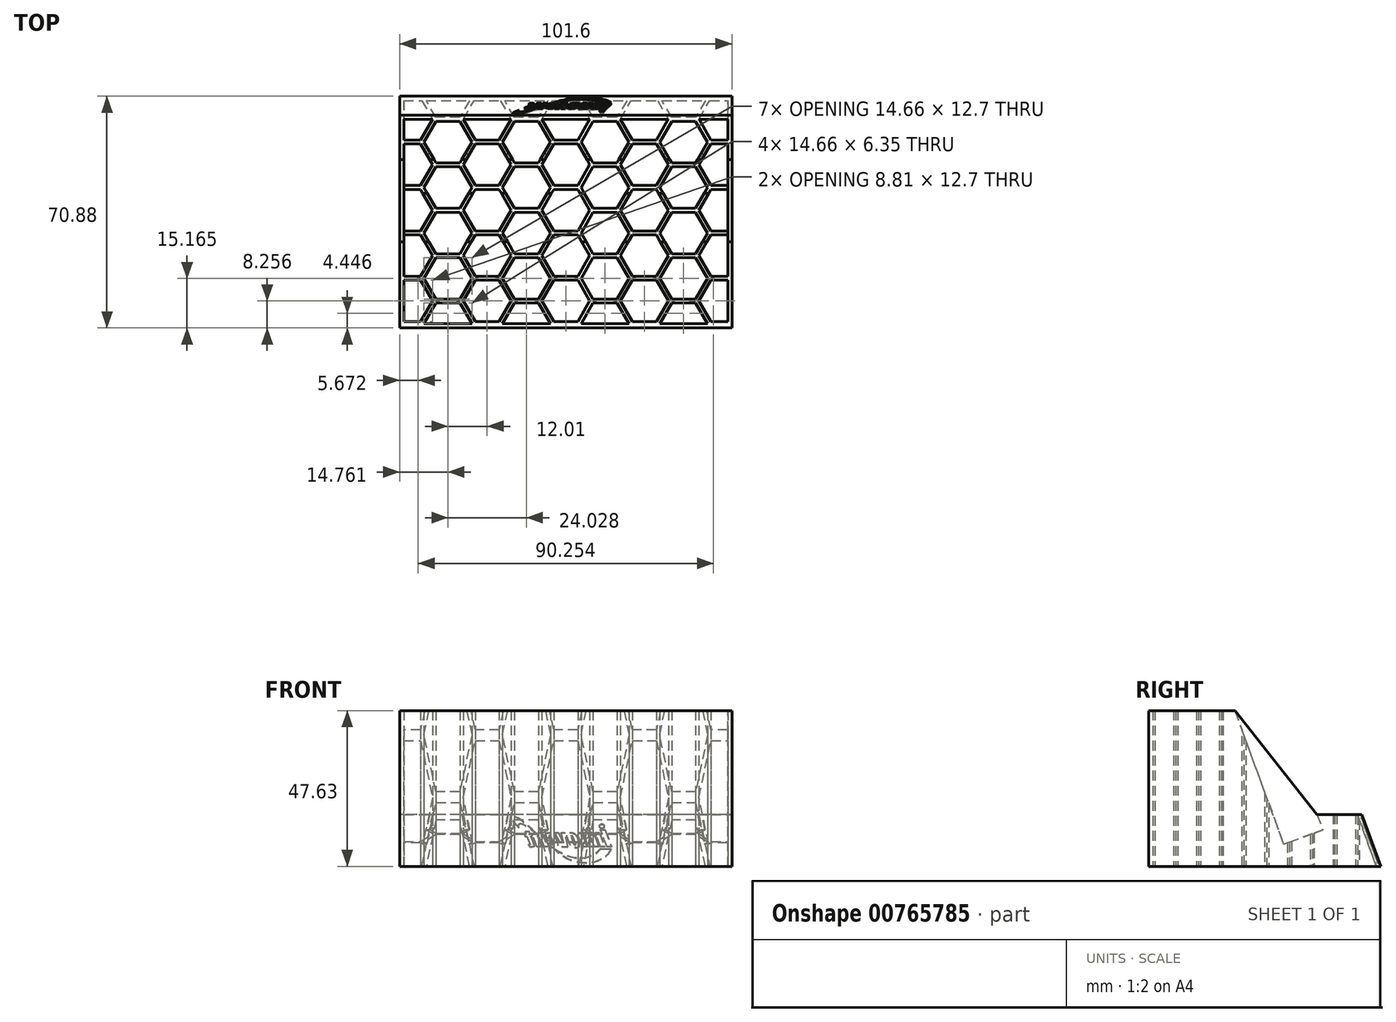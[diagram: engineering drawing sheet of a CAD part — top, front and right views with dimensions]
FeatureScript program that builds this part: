
annotation { "Feature Type Name" : "Feature", "Feature Type Description" : "" }
export const myFeature = defineFeature(function(context is Context, id is Id, definition is map)
    precondition{}
    {
        {
            var Q0;
            Q0=qCreatedBy(makeId("Top.planeOp"),FACE);
            var sketch = newSketch(context, id + "F0", { "sketchPlane" : qUnion([Q0])});
            skLineSegment(sketch, "E0.bottom", {"start": v(-69.85, 53.97) * mm, "end": v(69.85, 53.98) * mm});
            skLineSegment(sketch, "E0.top", {"start": v(-69.85, -47.63) * mm, "end": v(69.85, -47.62) * mm});
            skLineSegment(sketch, "E0.left", {"start": v(-69.85, 53.97) * mm, "end": v(-69.85, -47.63) * mm});
            skLineSegment(sketch, "E0.right", {"start": v(69.85, 53.98) * mm, "end": v(69.85, -47.62) * mm});
            skSolve(sketch);
        }
        {
            var Q0;
            Q0=makeQuery(id+"F0.imprint","IMPRINT",FACE,{"disambiguationData":[TD([[makeQuery(id+"F0.imprint","IMPRINT",EDGE,{"derivedFrom":sQuery(id+"F0.wireOp",EDGE,"E0.bottom")}),-1.0]])]});
            extrude(context, id + "F1", {"entities" : qUnion([Q0]), "depth" : 63.5 * mm, "offsetDistance" : 25.4 * mm});
        }
        {
            var Q0;
            Q0=qCreatedBy(makeId("Top.planeOp"),FACE);
            var sketch = newSketch(context, id + "F2", { "sketchPlane" : qUnion([Q0])});
            skCircle(sketch, "E1.cCircle", {"center": v(-61.25, 31.75) * mm, "radius": 6.35 * mm});
            skLineSegment(sketch, "E1.0", {"start": v(-57.58, 25.4) * mm, "end": v(-64.91, 25.4) * mm});
            skLineSegment(sketch, "E1.1", {"start": v(-64.91, 25.4) * mm, "end": v(-68.58, 31.75) * mm});
            skLineSegment(sketch, "E1.2", {"start": v(-68.58, 31.75) * mm, "end": v(-64.91, 38.1) * mm});
            skLineSegment(sketch, "E1.3", {"start": v(-64.91, 38.1) * mm, "end": v(-57.58, 38.1) * mm});
            skLineSegment(sketch, "E1.4", {"start": v(-57.58, 38.1) * mm, "end": v(-53.92, 31.75) * mm});
            skLineSegment(sketch, "E1.5", {"start": v(-53.92, 31.75) * mm, "end": v(-57.58, 25.4) * mm});
            skPoint(sketch, "E1.0.midPoint", {"position": v(-61.25, 25.4) * mm});
            skLineSegment(sketch, "E2.0.1.0", {"start": v(-64.91, 24.2) * mm, "end": v(-57.58, 24.2) * mm});
            skLineSegment(sketch, "E2.0.1.1", {"start": v(-68.58, 17.86) * mm, "end": v(-64.91, 24.2) * mm});
            skLineSegment(sketch, "E2.0.1.2", {"start": v(-64.91, 11.5) * mm, "end": v(-68.58, 17.86) * mm});
            skLineSegment(sketch, "E2.0.1.3", {"start": v(-57.58, 24.2) * mm, "end": v(-53.92, 17.86) * mm});
            skLineSegment(sketch, "E2.0.1.4", {"start": v(-53.92, 17.86) * mm, "end": v(-57.58, 11.5) * mm});
            skCircle(sketch, "E2.0.1.5", {"center": v(-61.25, 17.86) * mm, "radius": 6.35 * mm});
            skPoint(sketch, "E2.0.1.6", {"position": v(-61.25, 11.5) * mm});
            skLineSegment(sketch, "E2.0.1.7", {"start": v(-57.58, 11.5) * mm, "end": v(-64.91, 11.5) * mm});
            skLineSegment(sketch, "E2.0.2.0", {"start": v(-64.91, 10.31) * mm, "end": v(-57.58, 10.31) * mm});
            skLineSegment(sketch, "E2.0.2.1", {"start": v(-68.58, 3.96) * mm, "end": v(-64.91, 10.31) * mm});
            skLineSegment(sketch, "E2.0.2.2", {"start": v(-64.91, -2.39) * mm, "end": v(-68.58, 3.96) * mm});
            skLineSegment(sketch, "E2.0.2.3", {"start": v(-57.58, 10.31) * mm, "end": v(-53.92, 3.96) * mm});
            skLineSegment(sketch, "E2.0.2.4", {"start": v(-53.92, 3.96) * mm, "end": v(-57.58, -2.39) * mm});
            skCircle(sketch, "E2.0.2.5", {"center": v(-61.25, 3.96) * mm, "radius": 6.35 * mm});
            skPoint(sketch, "E2.0.2.6", {"position": v(-61.25, -2.39) * mm});
            skLineSegment(sketch, "E2.0.2.7", {"start": v(-57.58, -2.39) * mm, "end": v(-64.91, -2.39) * mm});
            skLineSegment(sketch, "E2.0.3.0", {"start": v(-64.91, -3.58) * mm, "end": v(-57.58, -3.58) * mm});
            skLineSegment(sketch, "E2.0.3.1", {"start": v(-68.58, -9.93) * mm, "end": v(-64.91, -3.58) * mm});
            skLineSegment(sketch, "E2.0.3.2", {"start": v(-64.91, -16.28) * mm, "end": v(-68.58, -9.93) * mm});
            skLineSegment(sketch, "E2.0.3.3", {"start": v(-57.58, -3.58) * mm, "end": v(-53.92, -9.93) * mm});
            skLineSegment(sketch, "E2.0.3.4", {"start": v(-53.92, -9.93) * mm, "end": v(-57.58, -16.28) * mm});
            skCircle(sketch, "E2.0.3.5", {"center": v(-61.25, -9.93) * mm, "radius": 6.35 * mm});
            skPoint(sketch, "E2.0.3.6", {"position": v(-61.25, -16.28) * mm});
            skLineSegment(sketch, "E2.0.3.7", {"start": v(-57.58, -16.28) * mm, "end": v(-64.91, -16.28) * mm});
            skLineSegment(sketch, "E2.0.4.0", {"start": v(-64.91, -17.48) * mm, "end": v(-57.58, -17.48) * mm});
            skLineSegment(sketch, "E2.0.4.1", {"start": v(-68.58, -23.83) * mm, "end": v(-64.91, -17.48) * mm});
            skLineSegment(sketch, "E2.0.4.2", {"start": v(-64.91, -30.18) * mm, "end": v(-68.58, -23.83) * mm});
            skLineSegment(sketch, "E2.0.4.3", {"start": v(-57.58, -17.48) * mm, "end": v(-53.92, -23.83) * mm});
            skLineSegment(sketch, "E2.0.4.4", {"start": v(-53.92, -23.83) * mm, "end": v(-57.58, -30.18) * mm});
            skCircle(sketch, "E2.0.4.5", {"center": v(-61.25, -23.83) * mm, "radius": 6.35 * mm});
            skPoint(sketch, "E2.0.4.6", {"position": v(-61.25, -30.18) * mm});
            skLineSegment(sketch, "E2.0.4.7", {"start": v(-57.58, -30.18) * mm, "end": v(-64.91, -30.18) * mm});
            skLineSegment(sketch, "E2.0.5.0", {"start": v(-64.91, -31.37) * mm, "end": v(-57.58, -31.37) * mm});
            skLineSegment(sketch, "E2.0.5.1", {"start": v(-68.58, -37.72) * mm, "end": v(-64.91, -31.37) * mm});
            skLineSegment(sketch, "E2.0.5.2", {"start": v(-64.91, -44.07) * mm, "end": v(-68.58, -37.72) * mm});
            skLineSegment(sketch, "E2.0.5.3", {"start": v(-57.58, -31.37) * mm, "end": v(-53.92, -37.72) * mm});
            skLineSegment(sketch, "E2.0.5.4", {"start": v(-53.92, -37.72) * mm, "end": v(-57.58, -44.07) * mm});
            skCircle(sketch, "E2.0.5.5", {"center": v(-61.25, -37.72) * mm, "radius": 6.35 * mm});
            skPoint(sketch, "E2.0.5.6", {"position": v(-61.25, -44.07) * mm});
            skLineSegment(sketch, "E2.0.5.7", {"start": v(-57.58, -44.07) * mm, "end": v(-64.91, -44.07) * mm});
            skLineSegment(sketch, "E2.1.0.0", {"start": v(-40.89, 38.1) * mm, "end": v(-33.55, 38.1) * mm});
            skLineSegment(sketch, "E2.1.0.1", {"start": v(-44.55, 31.75) * mm, "end": v(-40.89, 38.1) * mm});
            skLineSegment(sketch, "E2.1.0.2", {"start": v(-40.89, 25.4) * mm, "end": v(-44.55, 31.75) * mm});
            skLineSegment(sketch, "E2.1.0.3", {"start": v(-33.55, 38.1) * mm, "end": v(-29.89, 31.75) * mm});
            skLineSegment(sketch, "E2.1.0.4", {"start": v(-29.89, 31.75) * mm, "end": v(-33.55, 25.4) * mm});
            skCircle(sketch, "E2.1.0.5", {"center": v(-37.22, 31.75) * mm, "radius": 6.35 * mm});
            skPoint(sketch, "E2.1.0.6", {"position": v(-37.22, 25.4) * mm});
            skLineSegment(sketch, "E2.1.0.7", {"start": v(-33.55, 25.4) * mm, "end": v(-40.89, 25.4) * mm});
            skLineSegment(sketch, "E2.1.1.0", {"start": v(-40.89, 24.2) * mm, "end": v(-33.55, 24.2) * mm});
            skLineSegment(sketch, "E2.1.1.1", {"start": v(-44.55, 17.86) * mm, "end": v(-40.89, 24.2) * mm});
            skLineSegment(sketch, "E2.1.1.2", {"start": v(-40.89, 11.5) * mm, "end": v(-44.55, 17.86) * mm});
            skLineSegment(sketch, "E2.1.1.3", {"start": v(-33.55, 24.2) * mm, "end": v(-29.89, 17.86) * mm});
            skLineSegment(sketch, "E2.1.1.4", {"start": v(-29.89, 17.86) * mm, "end": v(-33.55, 11.5) * mm});
            skCircle(sketch, "E2.1.1.5", {"center": v(-37.22, 17.86) * mm, "radius": 6.35 * mm});
            skPoint(sketch, "E2.1.1.6", {"position": v(-37.22, 11.5) * mm});
            skLineSegment(sketch, "E2.1.1.7", {"start": v(-33.55, 11.5) * mm, "end": v(-40.89, 11.5) * mm});
            skLineSegment(sketch, "E2.1.2.0", {"start": v(-40.89, 10.31) * mm, "end": v(-33.55, 10.31) * mm});
            skLineSegment(sketch, "E2.1.2.1", {"start": v(-44.55, 3.96) * mm, "end": v(-40.89, 10.31) * mm});
            skLineSegment(sketch, "E2.1.2.2", {"start": v(-40.89, -2.39) * mm, "end": v(-44.55, 3.96) * mm});
            skLineSegment(sketch, "E2.1.2.3", {"start": v(-33.55, 10.31) * mm, "end": v(-29.89, 3.96) * mm});
            skLineSegment(sketch, "E2.1.2.4", {"start": v(-29.89, 3.96) * mm, "end": v(-33.55, -2.39) * mm});
            skCircle(sketch, "E2.1.2.5", {"center": v(-37.22, 3.96) * mm, "radius": 6.35 * mm});
            skPoint(sketch, "E2.1.2.6", {"position": v(-37.22, -2.39) * mm});
            skLineSegment(sketch, "E2.1.2.7", {"start": v(-33.55, -2.39) * mm, "end": v(-40.89, -2.39) * mm});
            skLineSegment(sketch, "E2.1.3.0", {"start": v(-40.89, -3.58) * mm, "end": v(-33.55, -3.58) * mm});
            skLineSegment(sketch, "E2.1.3.1", {"start": v(-44.55, -9.93) * mm, "end": v(-40.89, -3.58) * mm});
            skLineSegment(sketch, "E2.1.3.2", {"start": v(-40.89, -16.28) * mm, "end": v(-44.55, -9.93) * mm});
            skLineSegment(sketch, "E2.1.3.3", {"start": v(-33.55, -3.58) * mm, "end": v(-29.89, -9.93) * mm});
            skLineSegment(sketch, "E2.1.3.4", {"start": v(-29.89, -9.93) * mm, "end": v(-33.55, -16.28) * mm});
            skCircle(sketch, "E2.1.3.5", {"center": v(-37.22, -9.93) * mm, "radius": 6.35 * mm});
            skPoint(sketch, "E2.1.3.6", {"position": v(-37.22, -16.28) * mm});
            skLineSegment(sketch, "E2.1.3.7", {"start": v(-33.55, -16.28) * mm, "end": v(-40.89, -16.28) * mm});
            skLineSegment(sketch, "E2.1.4.0", {"start": v(-40.89, -17.48) * mm, "end": v(-33.55, -17.48) * mm});
            skLineSegment(sketch, "E2.1.4.1", {"start": v(-44.55, -23.83) * mm, "end": v(-40.89, -17.48) * mm});
            skLineSegment(sketch, "E2.1.4.2", {"start": v(-40.89, -30.18) * mm, "end": v(-44.55, -23.83) * mm});
            skLineSegment(sketch, "E2.1.4.3", {"start": v(-33.55, -17.48) * mm, "end": v(-29.89, -23.83) * mm});
            skLineSegment(sketch, "E2.1.4.4", {"start": v(-29.89, -23.83) * mm, "end": v(-33.55, -30.18) * mm});
            skCircle(sketch, "E2.1.4.5", {"center": v(-37.22, -23.83) * mm, "radius": 6.35 * mm});
            skPoint(sketch, "E2.1.4.6", {"position": v(-37.22, -30.18) * mm});
            skLineSegment(sketch, "E2.1.4.7", {"start": v(-33.55, -30.18) * mm, "end": v(-40.89, -30.18) * mm});
            skLineSegment(sketch, "E2.1.5.0", {"start": v(-40.89, -31.37) * mm, "end": v(-33.55, -31.37) * mm});
            skLineSegment(sketch, "E2.1.5.1", {"start": v(-44.55, -37.72) * mm, "end": v(-40.89, -31.37) * mm});
            skLineSegment(sketch, "E2.1.5.2", {"start": v(-40.89, -44.07) * mm, "end": v(-44.55, -37.72) * mm});
            skLineSegment(sketch, "E2.1.5.3", {"start": v(-33.55, -31.37) * mm, "end": v(-29.89, -37.72) * mm});
            skLineSegment(sketch, "E2.1.5.4", {"start": v(-29.89, -37.72) * mm, "end": v(-33.55, -44.07) * mm});
            skCircle(sketch, "E2.1.5.5", {"center": v(-37.22, -37.72) * mm, "radius": 6.35 * mm});
            skPoint(sketch, "E2.1.5.6", {"position": v(-37.22, -44.07) * mm});
            skLineSegment(sketch, "E2.1.5.7", {"start": v(-33.55, -44.07) * mm, "end": v(-40.89, -44.07) * mm});
            skLineSegment(sketch, "E2.2.0.0", {"start": v(-16.86, 38.1) * mm, "end": v(-9.52, 38.1) * mm});
            skLineSegment(sketch, "E2.2.0.1", {"start": v(-20.52, 31.75) * mm, "end": v(-16.86, 38.1) * mm});
            skLineSegment(sketch, "E2.2.0.2", {"start": v(-16.86, 25.4) * mm, "end": v(-20.52, 31.75) * mm});
            skLineSegment(sketch, "E2.2.0.3", {"start": v(-9.52, 38.1) * mm, "end": v(-5.86, 31.75) * mm});
            skLineSegment(sketch, "E2.2.0.4", {"start": v(-5.86, 31.75) * mm, "end": v(-9.52, 25.4) * mm});
            skCircle(sketch, "E2.2.0.5", {"center": v(-13.2, 31.75) * mm, "radius": 6.35 * mm});
            skPoint(sketch, "E2.2.0.6", {"position": v(-13.2, 25.4) * mm});
            skLineSegment(sketch, "E2.2.0.7", {"start": v(-9.52, 25.4) * mm, "end": v(-16.86, 25.4) * mm});
            skLineSegment(sketch, "E2.2.1.0", {"start": v(-16.86, 24.2) * mm, "end": v(-9.52, 24.2) * mm});
            skLineSegment(sketch, "E2.2.1.1", {"start": v(-20.52, 17.86) * mm, "end": v(-16.86, 24.2) * mm});
            skLineSegment(sketch, "E2.2.1.2", {"start": v(-16.86, 11.5) * mm, "end": v(-20.52, 17.86) * mm});
            skLineSegment(sketch, "E2.2.1.3", {"start": v(-9.52, 24.2) * mm, "end": v(-5.86, 17.86) * mm});
            skLineSegment(sketch, "E2.2.1.4", {"start": v(-5.86, 17.86) * mm, "end": v(-9.52, 11.5) * mm});
            skCircle(sketch, "E2.2.1.5", {"center": v(-13.2, 17.86) * mm, "radius": 6.35 * mm});
            skPoint(sketch, "E2.2.1.6", {"position": v(-13.2, 11.5) * mm});
            skLineSegment(sketch, "E2.2.1.7", {"start": v(-9.52, 11.5) * mm, "end": v(-16.86, 11.5) * mm});
            skLineSegment(sketch, "E2.2.2.0", {"start": v(-16.86, 10.31) * mm, "end": v(-9.52, 10.31) * mm});
            skLineSegment(sketch, "E2.2.2.1", {"start": v(-20.52, 3.96) * mm, "end": v(-16.86, 10.31) * mm});
            skLineSegment(sketch, "E2.2.2.2", {"start": v(-16.86, -2.39) * mm, "end": v(-20.52, 3.96) * mm});
            skLineSegment(sketch, "E2.2.2.3", {"start": v(-9.52, 10.31) * mm, "end": v(-5.86, 3.96) * mm});
            skLineSegment(sketch, "E2.2.2.4", {"start": v(-5.86, 3.96) * mm, "end": v(-9.52, -2.39) * mm});
            skCircle(sketch, "E2.2.2.5", {"center": v(-13.2, 3.96) * mm, "radius": 6.35 * mm});
            skPoint(sketch, "E2.2.2.6", {"position": v(-13.2, -2.39) * mm});
            skLineSegment(sketch, "E2.2.2.7", {"start": v(-9.52, -2.39) * mm, "end": v(-16.86, -2.39) * mm});
            skLineSegment(sketch, "E2.2.3.0", {"start": v(-16.86, -3.58) * mm, "end": v(-9.52, -3.58) * mm});
            skLineSegment(sketch, "E2.2.3.1", {"start": v(-20.52, -9.93) * mm, "end": v(-16.86, -3.58) * mm});
            skLineSegment(sketch, "E2.2.3.2", {"start": v(-16.86, -16.28) * mm, "end": v(-20.52, -9.93) * mm});
            skLineSegment(sketch, "E2.2.3.3", {"start": v(-9.52, -3.58) * mm, "end": v(-5.86, -9.93) * mm});
            skLineSegment(sketch, "E2.2.3.4", {"start": v(-5.86, -9.93) * mm, "end": v(-9.52, -16.28) * mm});
            skCircle(sketch, "E2.2.3.5", {"center": v(-13.2, -9.93) * mm, "radius": 6.35 * mm});
            skPoint(sketch, "E2.2.3.6", {"position": v(-13.2, -16.28) * mm});
            skLineSegment(sketch, "E2.2.3.7", {"start": v(-9.52, -16.28) * mm, "end": v(-16.86, -16.28) * mm});
            skLineSegment(sketch, "E2.2.4.0", {"start": v(-16.86, -17.48) * mm, "end": v(-9.52, -17.48) * mm});
            skLineSegment(sketch, "E2.2.4.1", {"start": v(-20.52, -23.83) * mm, "end": v(-16.86, -17.48) * mm});
            skLineSegment(sketch, "E2.2.4.2", {"start": v(-16.86, -30.18) * mm, "end": v(-20.52, -23.83) * mm});
            skLineSegment(sketch, "E2.2.4.3", {"start": v(-9.52, -17.48) * mm, "end": v(-5.86, -23.83) * mm});
            skLineSegment(sketch, "E2.2.4.4", {"start": v(-5.86, -23.83) * mm, "end": v(-9.52, -30.18) * mm});
            skCircle(sketch, "E2.2.4.5", {"center": v(-13.2, -23.83) * mm, "radius": 6.35 * mm});
            skPoint(sketch, "E2.2.4.6", {"position": v(-13.2, -30.18) * mm});
            skLineSegment(sketch, "E2.2.4.7", {"start": v(-9.52, -30.18) * mm, "end": v(-16.86, -30.18) * mm});
            skLineSegment(sketch, "E2.2.5.0", {"start": v(-16.86, -31.37) * mm, "end": v(-9.52, -31.37) * mm});
            skLineSegment(sketch, "E2.2.5.1", {"start": v(-20.52, -37.72) * mm, "end": v(-16.86, -31.37) * mm});
            skLineSegment(sketch, "E2.2.5.2", {"start": v(-16.86, -44.07) * mm, "end": v(-20.52, -37.72) * mm});
            skLineSegment(sketch, "E2.2.5.3", {"start": v(-9.52, -31.37) * mm, "end": v(-5.86, -37.72) * mm});
            skLineSegment(sketch, "E2.2.5.4", {"start": v(-5.86, -37.72) * mm, "end": v(-9.52, -44.07) * mm});
            skCircle(sketch, "E2.2.5.5", {"center": v(-13.2, -37.72) * mm, "radius": 6.35 * mm});
            skPoint(sketch, "E2.2.5.6", {"position": v(-13.2, -44.07) * mm});
            skLineSegment(sketch, "E2.2.5.7", {"start": v(-9.52, -44.07) * mm, "end": v(-16.86, -44.07) * mm});
            skLineSegment(sketch, "E2.3.0.0", {"start": v(7.17, 38.1) * mm, "end": v(14.5, 38.1) * mm});
            skLineSegment(sketch, "E2.3.0.1", {"start": v(3.5, 31.75) * mm, "end": v(7.17, 38.1) * mm});
            skLineSegment(sketch, "E2.3.0.2", {"start": v(7.17, 25.4) * mm, "end": v(3.5, 31.75) * mm});
            skLineSegment(sketch, "E2.3.0.3", {"start": v(14.5, 38.1) * mm, "end": v(18.17, 31.75) * mm});
            skLineSegment(sketch, "E2.3.0.4", {"start": v(18.17, 31.75) * mm, "end": v(14.5, 25.4) * mm});
            skCircle(sketch, "E2.3.0.5", {"center": v(10.84, 31.75) * mm, "radius": 6.35 * mm});
            skPoint(sketch, "E2.3.0.6", {"position": v(10.84, 25.4) * mm});
            skLineSegment(sketch, "E2.3.0.7", {"start": v(14.5, 25.4) * mm, "end": v(7.17, 25.4) * mm});
            skLineSegment(sketch, "E2.3.1.0", {"start": v(7.17, 24.2) * mm, "end": v(14.5, 24.2) * mm});
            skLineSegment(sketch, "E2.3.1.1", {"start": v(3.5, 17.86) * mm, "end": v(7.17, 24.2) * mm});
            skLineSegment(sketch, "E2.3.1.2", {"start": v(7.17, 11.5) * mm, "end": v(3.5, 17.86) * mm});
            skLineSegment(sketch, "E2.3.1.3", {"start": v(14.5, 24.2) * mm, "end": v(18.17, 17.86) * mm});
            skLineSegment(sketch, "E2.3.1.4", {"start": v(18.17, 17.86) * mm, "end": v(14.5, 11.5) * mm});
            skCircle(sketch, "E2.3.1.5", {"center": v(10.84, 17.86) * mm, "radius": 6.35 * mm});
            skPoint(sketch, "E2.3.1.6", {"position": v(10.84, 11.5) * mm});
            skLineSegment(sketch, "E2.3.1.7", {"start": v(14.5, 11.5) * mm, "end": v(7.17, 11.5) * mm});
            skLineSegment(sketch, "E2.3.2.0", {"start": v(7.17, 10.31) * mm, "end": v(14.5, 10.31) * mm});
            skLineSegment(sketch, "E2.3.2.1", {"start": v(3.5, 3.96) * mm, "end": v(7.17, 10.31) * mm});
            skLineSegment(sketch, "E2.3.2.2", {"start": v(7.17, -2.39) * mm, "end": v(3.5, 3.96) * mm});
            skLineSegment(sketch, "E2.3.2.3", {"start": v(14.5, 10.31) * mm, "end": v(18.17, 3.96) * mm});
            skLineSegment(sketch, "E2.3.2.4", {"start": v(18.17, 3.96) * mm, "end": v(14.5, -2.39) * mm});
            skCircle(sketch, "E2.3.2.5", {"center": v(10.84, 3.96) * mm, "radius": 6.35 * mm});
            skPoint(sketch, "E2.3.2.6", {"position": v(10.84, -2.39) * mm});
            skLineSegment(sketch, "E2.3.2.7", {"start": v(14.5, -2.39) * mm, "end": v(7.17, -2.39) * mm});
            skLineSegment(sketch, "E2.3.3.0", {"start": v(7.17, -3.58) * mm, "end": v(14.5, -3.58) * mm});
            skLineSegment(sketch, "E2.3.3.1", {"start": v(3.5, -9.93) * mm, "end": v(7.17, -3.58) * mm});
            skLineSegment(sketch, "E2.3.3.2", {"start": v(7.17, -16.28) * mm, "end": v(3.5, -9.93) * mm});
            skLineSegment(sketch, "E2.3.3.3", {"start": v(14.5, -3.58) * mm, "end": v(18.17, -9.93) * mm});
            skLineSegment(sketch, "E2.3.3.4", {"start": v(18.17, -9.93) * mm, "end": v(14.5, -16.28) * mm});
            skCircle(sketch, "E2.3.3.5", {"center": v(10.84, -9.93) * mm, "radius": 6.35 * mm});
            skPoint(sketch, "E2.3.3.6", {"position": v(10.84, -16.28) * mm});
            skLineSegment(sketch, "E2.3.3.7", {"start": v(14.5, -16.28) * mm, "end": v(7.17, -16.28) * mm});
            skLineSegment(sketch, "E2.3.4.0", {"start": v(7.17, -17.48) * mm, "end": v(14.5, -17.48) * mm});
            skLineSegment(sketch, "E2.3.4.1", {"start": v(3.5, -23.83) * mm, "end": v(7.17, -17.48) * mm});
            skLineSegment(sketch, "E2.3.4.2", {"start": v(7.17, -30.18) * mm, "end": v(3.5, -23.83) * mm});
            skLineSegment(sketch, "E2.3.4.3", {"start": v(14.5, -17.48) * mm, "end": v(18.17, -23.83) * mm});
            skLineSegment(sketch, "E2.3.4.4", {"start": v(18.17, -23.83) * mm, "end": v(14.5, -30.18) * mm});
            skCircle(sketch, "E2.3.4.5", {"center": v(10.84, -23.83) * mm, "radius": 6.35 * mm});
            skPoint(sketch, "E2.3.4.6", {"position": v(10.84, -30.18) * mm});
            skLineSegment(sketch, "E2.3.4.7", {"start": v(14.5, -30.18) * mm, "end": v(7.17, -30.18) * mm});
            skLineSegment(sketch, "E2.3.5.0", {"start": v(7.17, -31.37) * mm, "end": v(14.5, -31.37) * mm});
            skLineSegment(sketch, "E2.3.5.1", {"start": v(3.5, -37.72) * mm, "end": v(7.17, -31.37) * mm});
            skLineSegment(sketch, "E2.3.5.2", {"start": v(7.17, -44.07) * mm, "end": v(3.5, -37.72) * mm});
            skLineSegment(sketch, "E2.3.5.3", {"start": v(14.5, -31.37) * mm, "end": v(18.17, -37.72) * mm});
            skLineSegment(sketch, "E2.3.5.4", {"start": v(18.17, -37.72) * mm, "end": v(14.5, -44.07) * mm});
            skCircle(sketch, "E2.3.5.5", {"center": v(10.84, -37.72) * mm, "radius": 6.35 * mm});
            skPoint(sketch, "E2.3.5.6", {"position": v(10.84, -44.07) * mm});
            skLineSegment(sketch, "E2.3.5.7", {"start": v(14.5, -44.07) * mm, "end": v(7.17, -44.07) * mm});
            skLineSegment(sketch, "E2.4.0.0", {"start": v(31.2, 38.1) * mm, "end": v(38.53, 38.1) * mm});
            skLineSegment(sketch, "E2.4.0.1", {"start": v(27.53, 31.75) * mm, "end": v(31.2, 38.1) * mm});
            skLineSegment(sketch, "E2.4.0.2", {"start": v(31.2, 25.4) * mm, "end": v(27.53, 31.75) * mm});
            skLineSegment(sketch, "E2.4.0.3", {"start": v(38.53, 38.1) * mm, "end": v(42.2, 31.75) * mm});
            skLineSegment(sketch, "E2.4.0.4", {"start": v(42.2, 31.75) * mm, "end": v(38.53, 25.4) * mm});
            skCircle(sketch, "E2.4.0.5", {"center": v(34.87, 31.75) * mm, "radius": 6.35 * mm});
            skPoint(sketch, "E2.4.0.6", {"position": v(34.87, 25.4) * mm});
            skLineSegment(sketch, "E2.4.0.7", {"start": v(38.53, 25.4) * mm, "end": v(31.2, 25.4) * mm});
            skLineSegment(sketch, "E2.4.1.0", {"start": v(31.2, 24.2) * mm, "end": v(38.53, 24.2) * mm});
            skLineSegment(sketch, "E2.4.1.1", {"start": v(27.53, 17.86) * mm, "end": v(31.2, 24.2) * mm});
            skLineSegment(sketch, "E2.4.1.2", {"start": v(31.2, 11.5) * mm, "end": v(27.53, 17.86) * mm});
            skLineSegment(sketch, "E2.4.1.3", {"start": v(38.53, 24.2) * mm, "end": v(42.2, 17.86) * mm});
            skLineSegment(sketch, "E2.4.1.4", {"start": v(42.2, 17.86) * mm, "end": v(38.53, 11.5) * mm});
            skCircle(sketch, "E2.4.1.5", {"center": v(34.87, 17.86) * mm, "radius": 6.35 * mm});
            skPoint(sketch, "E2.4.1.6", {"position": v(34.87, 11.5) * mm});
            skLineSegment(sketch, "E2.4.1.7", {"start": v(38.53, 11.5) * mm, "end": v(31.2, 11.5) * mm});
            skLineSegment(sketch, "E2.4.2.0", {"start": v(31.2, 10.31) * mm, "end": v(38.53, 10.31) * mm});
            skLineSegment(sketch, "E2.4.2.1", {"start": v(27.53, 3.96) * mm, "end": v(31.2, 10.31) * mm});
            skLineSegment(sketch, "E2.4.2.2", {"start": v(31.2, -2.39) * mm, "end": v(27.53, 3.96) * mm});
            skLineSegment(sketch, "E2.4.2.3", {"start": v(38.53, 10.31) * mm, "end": v(42.2, 3.96) * mm});
            skLineSegment(sketch, "E2.4.2.4", {"start": v(42.2, 3.96) * mm, "end": v(38.53, -2.39) * mm});
            skCircle(sketch, "E2.4.2.5", {"center": v(34.87, 3.96) * mm, "radius": 6.35 * mm});
            skPoint(sketch, "E2.4.2.6", {"position": v(34.87, -2.39) * mm});
            skLineSegment(sketch, "E2.4.2.7", {"start": v(38.53, -2.39) * mm, "end": v(31.2, -2.39) * mm});
            skLineSegment(sketch, "E2.4.3.0", {"start": v(31.2, -3.58) * mm, "end": v(38.53, -3.58) * mm});
            skLineSegment(sketch, "E2.4.3.1", {"start": v(27.53, -9.93) * mm, "end": v(31.2, -3.58) * mm});
            skLineSegment(sketch, "E2.4.3.2", {"start": v(31.2, -16.28) * mm, "end": v(27.53, -9.93) * mm});
            skLineSegment(sketch, "E2.4.3.3", {"start": v(38.53, -3.58) * mm, "end": v(42.2, -9.93) * mm});
            skLineSegment(sketch, "E2.4.3.4", {"start": v(42.2, -9.93) * mm, "end": v(38.53, -16.28) * mm});
            skCircle(sketch, "E2.4.3.5", {"center": v(34.87, -9.93) * mm, "radius": 6.35 * mm});
            skPoint(sketch, "E2.4.3.6", {"position": v(34.87, -16.28) * mm});
            skLineSegment(sketch, "E2.4.3.7", {"start": v(38.53, -16.28) * mm, "end": v(31.2, -16.28) * mm});
            skLineSegment(sketch, "E2.4.4.0", {"start": v(31.2, -17.48) * mm, "end": v(38.53, -17.48) * mm});
            skLineSegment(sketch, "E2.4.4.1", {"start": v(27.53, -23.83) * mm, "end": v(31.2, -17.48) * mm});
            skLineSegment(sketch, "E2.4.4.2", {"start": v(31.2, -30.18) * mm, "end": v(27.53, -23.83) * mm});
            skLineSegment(sketch, "E2.4.4.3", {"start": v(38.53, -17.48) * mm, "end": v(42.2, -23.83) * mm});
            skLineSegment(sketch, "E2.4.4.4", {"start": v(42.2, -23.83) * mm, "end": v(38.53, -30.18) * mm});
            skCircle(sketch, "E2.4.4.5", {"center": v(34.87, -23.83) * mm, "radius": 6.35 * mm});
            skPoint(sketch, "E2.4.4.6", {"position": v(34.87, -30.18) * mm});
            skLineSegment(sketch, "E2.4.4.7", {"start": v(38.53, -30.18) * mm, "end": v(31.2, -30.18) * mm});
            skLineSegment(sketch, "E2.4.5.0", {"start": v(31.2, -31.37) * mm, "end": v(38.53, -31.37) * mm});
            skLineSegment(sketch, "E2.4.5.1", {"start": v(27.53, -37.72) * mm, "end": v(31.2, -31.37) * mm});
            skLineSegment(sketch, "E2.4.5.2", {"start": v(31.2, -44.07) * mm, "end": v(27.53, -37.72) * mm});
            skLineSegment(sketch, "E2.4.5.3", {"start": v(38.53, -31.37) * mm, "end": v(42.2, -37.72) * mm});
            skLineSegment(sketch, "E2.4.5.4", {"start": v(42.2, -37.72) * mm, "end": v(38.53, -44.07) * mm});
            skCircle(sketch, "E2.4.5.5", {"center": v(34.87, -37.72) * mm, "radius": 6.35 * mm});
            skPoint(sketch, "E2.4.5.6", {"position": v(34.87, -44.07) * mm});
            skLineSegment(sketch, "E2.4.5.7", {"start": v(38.53, -44.07) * mm, "end": v(31.2, -44.07) * mm});
            skLineSegment(sketch, "E2.5.0.0", {"start": v(55.23, 38.1) * mm, "end": v(62.56, 38.1) * mm});
            skLineSegment(sketch, "E2.5.0.1", {"start": v(51.56, 31.75) * mm, "end": v(55.23, 38.1) * mm});
            skLineSegment(sketch, "E2.5.0.2", {"start": v(55.23, 25.4) * mm, "end": v(51.56, 31.75) * mm});
            skLineSegment(sketch, "E2.5.0.3", {"start": v(62.56, 38.1) * mm, "end": v(66.23, 31.75) * mm});
            skLineSegment(sketch, "E2.5.0.4", {"start": v(66.23, 31.75) * mm, "end": v(62.56, 25.4) * mm});
            skCircle(sketch, "E2.5.0.5", {"center": v(58.9, 31.75) * mm, "radius": 6.35 * mm});
            skPoint(sketch, "E2.5.0.6", {"position": v(58.9, 25.4) * mm});
            skLineSegment(sketch, "E2.5.0.7", {"start": v(62.56, 25.4) * mm, "end": v(55.23, 25.4) * mm});
            skLineSegment(sketch, "E2.5.1.0", {"start": v(55.23, 24.2) * mm, "end": v(62.56, 24.2) * mm});
            skLineSegment(sketch, "E2.5.1.1", {"start": v(51.56, 17.86) * mm, "end": v(55.23, 24.2) * mm});
            skLineSegment(sketch, "E2.5.1.2", {"start": v(55.23, 11.5) * mm, "end": v(51.56, 17.86) * mm});
            skLineSegment(sketch, "E2.5.1.3", {"start": v(62.56, 24.2) * mm, "end": v(66.23, 17.86) * mm});
            skLineSegment(sketch, "E2.5.1.4", {"start": v(66.23, 17.86) * mm, "end": v(62.56, 11.5) * mm});
            skCircle(sketch, "E2.5.1.5", {"center": v(58.9, 17.86) * mm, "radius": 6.35 * mm});
            skPoint(sketch, "E2.5.1.6", {"position": v(58.9, 11.5) * mm});
            skLineSegment(sketch, "E2.5.1.7", {"start": v(62.56, 11.5) * mm, "end": v(55.23, 11.5) * mm});
            skLineSegment(sketch, "E2.5.2.0", {"start": v(55.23, 10.31) * mm, "end": v(62.56, 10.31) * mm});
            skLineSegment(sketch, "E2.5.2.1", {"start": v(51.56, 3.96) * mm, "end": v(55.23, 10.31) * mm});
            skLineSegment(sketch, "E2.5.2.2", {"start": v(55.23, -2.39) * mm, "end": v(51.56, 3.96) * mm});
            skLineSegment(sketch, "E2.5.2.3", {"start": v(62.56, 10.31) * mm, "end": v(66.23, 3.96) * mm});
            skLineSegment(sketch, "E2.5.2.4", {"start": v(66.23, 3.96) * mm, "end": v(62.56, -2.39) * mm});
            skCircle(sketch, "E2.5.2.5", {"center": v(58.9, 3.96) * mm, "radius": 6.35 * mm});
            skPoint(sketch, "E2.5.2.6", {"position": v(58.9, -2.39) * mm});
            skLineSegment(sketch, "E2.5.2.7", {"start": v(62.56, -2.39) * mm, "end": v(55.23, -2.39) * mm});
            skLineSegment(sketch, "E2.5.3.0", {"start": v(55.23, -3.58) * mm, "end": v(62.56, -3.58) * mm});
            skLineSegment(sketch, "E2.5.3.1", {"start": v(51.56, -9.93) * mm, "end": v(55.23, -3.58) * mm});
            skLineSegment(sketch, "E2.5.3.2", {"start": v(55.23, -16.28) * mm, "end": v(51.56, -9.93) * mm});
            skLineSegment(sketch, "E2.5.3.3", {"start": v(62.56, -3.58) * mm, "end": v(66.23, -9.93) * mm});
            skLineSegment(sketch, "E2.5.3.4", {"start": v(66.23, -9.93) * mm, "end": v(62.56, -16.28) * mm});
            skCircle(sketch, "E2.5.3.5", {"center": v(58.9, -9.93) * mm, "radius": 6.35 * mm});
            skPoint(sketch, "E2.5.3.6", {"position": v(58.9, -16.28) * mm});
            skLineSegment(sketch, "E2.5.3.7", {"start": v(62.56, -16.28) * mm, "end": v(55.23, -16.28) * mm});
            skLineSegment(sketch, "E2.5.4.0", {"start": v(55.23, -17.48) * mm, "end": v(62.56, -17.48) * mm});
            skLineSegment(sketch, "E2.5.4.1", {"start": v(51.56, -23.83) * mm, "end": v(55.23, -17.48) * mm});
            skLineSegment(sketch, "E2.5.4.2", {"start": v(55.23, -30.18) * mm, "end": v(51.56, -23.83) * mm});
            skLineSegment(sketch, "E2.5.4.3", {"start": v(62.56, -17.48) * mm, "end": v(66.23, -23.83) * mm});
            skLineSegment(sketch, "E2.5.4.4", {"start": v(66.23, -23.83) * mm, "end": v(62.56, -30.18) * mm});
            skCircle(sketch, "E2.5.4.5", {"center": v(58.9, -23.83) * mm, "radius": 6.35 * mm});
            skPoint(sketch, "E2.5.4.6", {"position": v(58.9, -30.18) * mm});
            skLineSegment(sketch, "E2.5.4.7", {"start": v(62.56, -30.18) * mm, "end": v(55.23, -30.18) * mm});
            skLineSegment(sketch, "E2.5.5.0", {"start": v(55.23, -31.37) * mm, "end": v(62.56, -31.37) * mm});
            skLineSegment(sketch, "E2.5.5.1", {"start": v(51.56, -37.72) * mm, "end": v(55.23, -31.37) * mm});
            skLineSegment(sketch, "E2.5.5.2", {"start": v(55.23, -44.07) * mm, "end": v(51.56, -37.72) * mm});
            skLineSegment(sketch, "E2.5.5.3", {"start": v(62.56, -31.37) * mm, "end": v(66.23, -37.72) * mm});
            skLineSegment(sketch, "E2.5.5.4", {"start": v(66.23, -37.72) * mm, "end": v(62.56, -44.07) * mm});
            skCircle(sketch, "E2.5.5.5", {"center": v(58.9, -37.72) * mm, "radius": 6.35 * mm});
            skPoint(sketch, "E2.5.5.6", {"position": v(58.9, -44.07) * mm});
            skLineSegment(sketch, "E2.5.5.7", {"start": v(62.56, -44.07) * mm, "end": v(55.23, -44.07) * mm});
            skLineSegment(sketch, "E2.direction1", {"start": v(-64.91, 25.4) * mm, "end": v(-40.89, 25.4) * mm, "construction": true});
            skLineSegment(sketch, "E2.direction2", {"start": v(-64.91, 25.4) * mm, "end": v(-64.91, 11.5) * mm, "construction": true});
            skCircle(sketch, "E3.cCircle", {"center": v(-49.24, 38.73) * mm, "radius": 6.35 * mm, "construction": true});
            skLineSegment(sketch, "E3.0", {"start": v(-45.57, 32.38) * mm, "end": v(-52.9, 32.38) * mm});
            skLineSegment(sketch, "E3.1", {"start": v(-52.9, 32.38) * mm, "end": v(-56.57, 38.73) * mm});
            skLineSegment(sketch, "E3.2", {"start": v(-56.57, 38.73) * mm, "end": v(-52.9, 45.09) * mm});
            skLineSegment(sketch, "E3.3", {"start": v(-52.9, 45.09) * mm, "end": v(-45.57, 45.09) * mm});
            skLineSegment(sketch, "E3.4", {"start": v(-45.57, 45.09) * mm, "end": v(-41.9, 38.73) * mm});
            skLineSegment(sketch, "E3.5", {"start": v(-41.9, 38.73) * mm, "end": v(-45.57, 32.38) * mm});
            skPoint(sketch, "E3.0.midPoint", {"position": v(-49.24, 32.38) * mm});
            skPoint(sketch, "E4.0.1.0", {"position": v(-49.24, 18.5) * mm});
            skLineSegment(sketch, "E4.0.1.1", {"start": v(-41.9, 24.84) * mm, "end": v(-45.57, 18.5) * mm});
            skLineSegment(sketch, "E4.0.1.2", {"start": v(-45.57, 31.2) * mm, "end": v(-41.9, 24.84) * mm});
            skLineSegment(sketch, "E4.0.1.3", {"start": v(-52.9, 31.2) * mm, "end": v(-45.57, 31.2) * mm});
            skLineSegment(sketch, "E4.0.1.4", {"start": v(-56.57, 24.84) * mm, "end": v(-52.9, 31.2) * mm});
            skLineSegment(sketch, "E4.0.1.5", {"start": v(-52.9, 18.5) * mm, "end": v(-56.57, 24.84) * mm});
            skLineSegment(sketch, "E4.0.1.6", {"start": v(-45.57, 18.5) * mm, "end": v(-52.9, 18.5) * mm});
            skCircle(sketch, "E4.0.1.7", {"center": v(-49.24, 24.84) * mm, "radius": 6.35 * mm, "construction": true});
            skPoint(sketch, "E4.0.2.0", {"position": v(-49.24, 4.6) * mm});
            skLineSegment(sketch, "E4.0.2.1", {"start": v(-41.9, 10.95) * mm, "end": v(-45.57, 4.6) * mm});
            skLineSegment(sketch, "E4.0.2.2", {"start": v(-45.57, 17.3) * mm, "end": v(-41.9, 10.95) * mm});
            skLineSegment(sketch, "E4.0.2.3", {"start": v(-52.9, 17.3) * mm, "end": v(-45.57, 17.3) * mm});
            skLineSegment(sketch, "E4.0.2.4", {"start": v(-56.57, 10.95) * mm, "end": v(-52.9, 17.3) * mm});
            skLineSegment(sketch, "E4.0.2.5", {"start": v(-52.9, 4.6) * mm, "end": v(-56.57, 10.95) * mm});
            skLineSegment(sketch, "E4.0.2.6", {"start": v(-45.57, 4.6) * mm, "end": v(-52.9, 4.6) * mm});
            skCircle(sketch, "E4.0.2.7", {"center": v(-49.24, 10.95) * mm, "radius": 6.35 * mm, "construction": true});
            skPoint(sketch, "E4.0.3.0", {"position": v(-49.24, -9.3) * mm});
            skLineSegment(sketch, "E4.0.3.1", {"start": v(-41.9, -2.95) * mm, "end": v(-45.57, -9.3) * mm});
            skLineSegment(sketch, "E4.0.3.2", {"start": v(-45.57, 3.4) * mm, "end": v(-41.9, -2.95) * mm});
            skLineSegment(sketch, "E4.0.3.3", {"start": v(-52.9, 3.4) * mm, "end": v(-45.57, 3.4) * mm});
            skLineSegment(sketch, "E4.0.3.4", {"start": v(-56.57, -2.95) * mm, "end": v(-52.9, 3.4) * mm});
            skLineSegment(sketch, "E4.0.3.5", {"start": v(-52.9, -9.3) * mm, "end": v(-56.57, -2.95) * mm});
            skLineSegment(sketch, "E4.0.3.6", {"start": v(-45.57, -9.3) * mm, "end": v(-52.9, -9.3) * mm});
            skCircle(sketch, "E4.0.3.7", {"center": v(-49.24, -2.95) * mm, "radius": 6.35 * mm, "construction": true});
            skPoint(sketch, "E4.0.4.0", {"position": v(-49.24, -23.2) * mm});
            skLineSegment(sketch, "E4.0.4.1", {"start": v(-41.9, -16.84) * mm, "end": v(-45.57, -23.2) * mm});
            skLineSegment(sketch, "E4.0.4.2", {"start": v(-45.57, -10.5) * mm, "end": v(-41.9, -16.84) * mm});
            skLineSegment(sketch, "E4.0.4.3", {"start": v(-52.9, -10.5) * mm, "end": v(-45.57, -10.5) * mm});
            skLineSegment(sketch, "E4.0.4.4", {"start": v(-56.57, -16.84) * mm, "end": v(-52.9, -10.5) * mm});
            skLineSegment(sketch, "E4.0.4.5", {"start": v(-52.9, -23.2) * mm, "end": v(-56.57, -16.84) * mm});
            skLineSegment(sketch, "E4.0.4.6", {"start": v(-45.57, -23.2) * mm, "end": v(-52.9, -23.2) * mm});
            skCircle(sketch, "E4.0.4.7", {"center": v(-49.24, -16.84) * mm, "radius": 6.35 * mm, "construction": true});
            skPoint(sketch, "E4.0.5.0", {"position": v(-49.24, -37.08) * mm});
            skLineSegment(sketch, "E4.0.5.1", {"start": v(-41.9, -30.73) * mm, "end": v(-45.57, -37.08) * mm});
            skLineSegment(sketch, "E4.0.5.2", {"start": v(-45.57, -24.38) * mm, "end": v(-41.9, -30.73) * mm});
            skLineSegment(sketch, "E4.0.5.3", {"start": v(-52.9, -24.38) * mm, "end": v(-45.57, -24.38) * mm});
            skLineSegment(sketch, "E4.0.5.4", {"start": v(-56.57, -30.73) * mm, "end": v(-52.9, -24.38) * mm});
            skLineSegment(sketch, "E4.0.5.5", {"start": v(-52.9, -37.08) * mm, "end": v(-56.57, -30.73) * mm});
            skLineSegment(sketch, "E4.0.5.6", {"start": v(-45.57, -37.08) * mm, "end": v(-52.9, -37.08) * mm});
            skCircle(sketch, "E4.0.5.7", {"center": v(-49.24, -30.73) * mm, "radius": 6.35 * mm, "construction": true});
            skPoint(sketch, "E4.1.0.0", {"position": v(-25.2, 32.38) * mm});
            skLineSegment(sketch, "E4.1.0.1", {"start": v(-17.88, 38.74) * mm, "end": v(-21.54, 32.39) * mm});
            skLineSegment(sketch, "E4.1.0.2", {"start": v(-21.54, 45.09) * mm, "end": v(-17.88, 38.74) * mm});
            skLineSegment(sketch, "E4.1.0.3", {"start": v(-28.88, 45.09) * mm, "end": v(-21.54, 45.09) * mm});
            skLineSegment(sketch, "E4.1.0.4", {"start": v(-32.54, 38.74) * mm, "end": v(-28.88, 45.09) * mm});
            skLineSegment(sketch, "E4.1.0.5", {"start": v(-28.88, 32.39) * mm, "end": v(-32.54, 38.73) * mm});
            skLineSegment(sketch, "E4.1.0.6", {"start": v(-21.54, 32.38) * mm, "end": v(-28.88, 32.38) * mm});
            skCircle(sketch, "E4.1.0.7", {"center": v(-25.2, 38.73) * mm, "radius": 6.35 * mm, "construction": true});
            skPoint(sketch, "E4.1.1.0", {"position": v(-25.2, 18.5) * mm});
            skLineSegment(sketch, "E4.1.1.1", {"start": v(-17.88, 24.84) * mm, "end": v(-21.54, 18.5) * mm});
            skLineSegment(sketch, "E4.1.1.2", {"start": v(-21.54, 31.2) * mm, "end": v(-17.88, 24.84) * mm});
            skLineSegment(sketch, "E4.1.1.3", {"start": v(-28.88, 31.2) * mm, "end": v(-21.54, 31.2) * mm});
            skLineSegment(sketch, "E4.1.1.4", {"start": v(-32.54, 24.84) * mm, "end": v(-28.88, 31.2) * mm});
            skLineSegment(sketch, "E4.1.1.5", {"start": v(-28.88, 18.5) * mm, "end": v(-32.54, 24.84) * mm});
            skLineSegment(sketch, "E4.1.1.6", {"start": v(-21.54, 18.5) * mm, "end": v(-28.88, 18.5) * mm});
            skCircle(sketch, "E4.1.1.7", {"center": v(-25.2, 24.84) * mm, "radius": 6.35 * mm, "construction": true});
            skPoint(sketch, "E4.1.2.0", {"position": v(-25.2, 4.6) * mm});
            skLineSegment(sketch, "E4.1.2.1", {"start": v(-17.88, 10.95) * mm, "end": v(-21.54, 4.6) * mm});
            skLineSegment(sketch, "E4.1.2.2", {"start": v(-21.54, 17.3) * mm, "end": v(-17.88, 10.95) * mm});
            skLineSegment(sketch, "E4.1.2.3", {"start": v(-28.88, 17.3) * mm, "end": v(-21.54, 17.3) * mm});
            skLineSegment(sketch, "E4.1.2.4", {"start": v(-32.54, 10.95) * mm, "end": v(-28.88, 17.3) * mm});
            skLineSegment(sketch, "E4.1.2.5", {"start": v(-28.88, 4.6) * mm, "end": v(-32.54, 10.95) * mm});
            skLineSegment(sketch, "E4.1.2.6", {"start": v(-21.54, 4.6) * mm, "end": v(-28.88, 4.6) * mm});
            skCircle(sketch, "E4.1.2.7", {"center": v(-25.2, 10.95) * mm, "radius": 6.35 * mm, "construction": true});
            skPoint(sketch, "E4.1.3.0", {"position": v(-25.2, -9.3) * mm});
            skLineSegment(sketch, "E4.1.3.1", {"start": v(-17.88, -2.95) * mm, "end": v(-21.54, -9.3) * mm});
            skLineSegment(sketch, "E4.1.3.2", {"start": v(-21.54, 3.4) * mm, "end": v(-17.88, -2.95) * mm});
            skLineSegment(sketch, "E4.1.3.3", {"start": v(-28.88, 3.4) * mm, "end": v(-21.54, 3.4) * mm});
            skLineSegment(sketch, "E4.1.3.4", {"start": v(-32.54, -2.95) * mm, "end": v(-28.88, 3.4) * mm});
            skLineSegment(sketch, "E4.1.3.5", {"start": v(-28.88, -9.3) * mm, "end": v(-32.54, -2.95) * mm});
            skLineSegment(sketch, "E4.1.3.6", {"start": v(-21.54, -9.3) * mm, "end": v(-28.88, -9.3) * mm});
            skCircle(sketch, "E4.1.3.7", {"center": v(-25.2, -2.95) * mm, "radius": 6.35 * mm, "construction": true});
            skPoint(sketch, "E4.1.4.0", {"position": v(-25.2, -23.2) * mm});
            skLineSegment(sketch, "E4.1.4.1", {"start": v(-17.88, -16.84) * mm, "end": v(-21.54, -23.2) * mm});
            skLineSegment(sketch, "E4.1.4.2", {"start": v(-21.54, -10.5) * mm, "end": v(-17.88, -16.84) * mm});
            skLineSegment(sketch, "E4.1.4.3", {"start": v(-28.88, -10.5) * mm, "end": v(-21.54, -10.5) * mm});
            skLineSegment(sketch, "E4.1.4.4", {"start": v(-32.54, -16.84) * mm, "end": v(-28.88, -10.5) * mm});
            skLineSegment(sketch, "E4.1.4.5", {"start": v(-28.88, -23.2) * mm, "end": v(-32.54, -16.84) * mm});
            skLineSegment(sketch, "E4.1.4.6", {"start": v(-21.54, -23.2) * mm, "end": v(-28.88, -23.2) * mm});
            skCircle(sketch, "E4.1.4.7", {"center": v(-25.2, -16.84) * mm, "radius": 6.35 * mm, "construction": true});
            skPoint(sketch, "E4.1.5.0", {"position": v(-25.2, -37.08) * mm});
            skLineSegment(sketch, "E4.1.5.1", {"start": v(-17.88, -30.73) * mm, "end": v(-21.54, -37.08) * mm});
            skLineSegment(sketch, "E4.1.5.2", {"start": v(-21.54, -24.38) * mm, "end": v(-17.88, -30.73) * mm});
            skLineSegment(sketch, "E4.1.5.3", {"start": v(-28.88, -24.38) * mm, "end": v(-21.54, -24.38) * mm});
            skLineSegment(sketch, "E4.1.5.4", {"start": v(-32.54, -30.73) * mm, "end": v(-28.88, -24.38) * mm});
            skLineSegment(sketch, "E4.1.5.5", {"start": v(-28.88, -37.08) * mm, "end": v(-32.54, -30.73) * mm});
            skLineSegment(sketch, "E4.1.5.6", {"start": v(-21.54, -37.08) * mm, "end": v(-28.88, -37.08) * mm});
            skCircle(sketch, "E4.1.5.7", {"center": v(-25.2, -30.73) * mm, "radius": 6.35 * mm, "construction": true});
            skPoint(sketch, "E4.2.0.0", {"position": v(-1.18, 32.38) * mm});
            skLineSegment(sketch, "E4.2.0.1", {"start": v(6.15, 38.74) * mm, "end": v(2.49, 32.39) * mm});
            skLineSegment(sketch, "E4.2.0.2", {"start": v(2.49, 45.09) * mm, "end": v(6.15, 38.74) * mm});
            skLineSegment(sketch, "E4.2.0.3", {"start": v(-4.85, 45.09) * mm, "end": v(2.49, 45.09) * mm});
            skLineSegment(sketch, "E4.2.0.4", {"start": v(-8.51, 38.74) * mm, "end": v(-4.85, 45.09) * mm});
            skLineSegment(sketch, "E4.2.0.5", {"start": v(-4.85, 32.39) * mm, "end": v(-8.51, 38.73) * mm});
            skLineSegment(sketch, "E4.2.0.6", {"start": v(2.49, 32.38) * mm, "end": v(-4.85, 32.38) * mm});
            skCircle(sketch, "E4.2.0.7", {"center": v(-1.18, 38.73) * mm, "radius": 6.35 * mm, "construction": true});
            skPoint(sketch, "E4.2.1.0", {"position": v(-1.18, 18.5) * mm});
            skLineSegment(sketch, "E4.2.1.1", {"start": v(6.15, 24.84) * mm, "end": v(2.49, 18.5) * mm});
            skLineSegment(sketch, "E4.2.1.2", {"start": v(2.49, 31.2) * mm, "end": v(6.15, 24.84) * mm});
            skLineSegment(sketch, "E4.2.1.3", {"start": v(-4.85, 31.2) * mm, "end": v(2.49, 31.2) * mm});
            skLineSegment(sketch, "E4.2.1.4", {"start": v(-8.51, 24.84) * mm, "end": v(-4.85, 31.2) * mm});
            skLineSegment(sketch, "E4.2.1.5", {"start": v(-4.85, 18.5) * mm, "end": v(-8.51, 24.84) * mm});
            skLineSegment(sketch, "E4.2.1.6", {"start": v(2.49, 18.5) * mm, "end": v(-4.85, 18.5) * mm});
            skCircle(sketch, "E4.2.1.7", {"center": v(-1.18, 24.84) * mm, "radius": 6.35 * mm, "construction": true});
            skPoint(sketch, "E4.2.2.0", {"position": v(-1.18, 4.6) * mm});
            skLineSegment(sketch, "E4.2.2.1", {"start": v(6.15, 10.95) * mm, "end": v(2.49, 4.6) * mm});
            skLineSegment(sketch, "E4.2.2.2", {"start": v(2.49, 17.3) * mm, "end": v(6.15, 10.95) * mm});
            skLineSegment(sketch, "E4.2.2.3", {"start": v(-4.85, 17.3) * mm, "end": v(2.49, 17.3) * mm});
            skLineSegment(sketch, "E4.2.2.4", {"start": v(-8.51, 10.95) * mm, "end": v(-4.85, 17.3) * mm});
            skLineSegment(sketch, "E4.2.2.5", {"start": v(-4.85, 4.6) * mm, "end": v(-8.51, 10.95) * mm});
            skLineSegment(sketch, "E4.2.2.6", {"start": v(2.49, 4.6) * mm, "end": v(-4.85, 4.6) * mm});
            skCircle(sketch, "E4.2.2.7", {"center": v(-1.18, 10.95) * mm, "radius": 6.35 * mm, "construction": true});
            skPoint(sketch, "E4.2.3.0", {"position": v(-1.18, -9.3) * mm});
            skLineSegment(sketch, "E4.2.3.1", {"start": v(6.15, -2.95) * mm, "end": v(2.49, -9.3) * mm});
            skLineSegment(sketch, "E4.2.3.2", {"start": v(2.49, 3.4) * mm, "end": v(6.15, -2.95) * mm});
            skLineSegment(sketch, "E4.2.3.3", {"start": v(-4.85, 3.4) * mm, "end": v(2.49, 3.4) * mm});
            skLineSegment(sketch, "E4.2.3.4", {"start": v(-8.51, -2.95) * mm, "end": v(-4.85, 3.4) * mm});
            skLineSegment(sketch, "E4.2.3.5", {"start": v(-4.85, -9.3) * mm, "end": v(-8.51, -2.95) * mm});
            skLineSegment(sketch, "E4.2.3.6", {"start": v(2.49, -9.3) * mm, "end": v(-4.85, -9.3) * mm});
            skCircle(sketch, "E4.2.3.7", {"center": v(-1.18, -2.95) * mm, "radius": 6.35 * mm, "construction": true});
            skPoint(sketch, "E4.2.4.0", {"position": v(-1.18, -23.2) * mm});
            skLineSegment(sketch, "E4.2.4.1", {"start": v(6.15, -16.84) * mm, "end": v(2.49, -23.2) * mm});
            skLineSegment(sketch, "E4.2.4.2", {"start": v(2.49, -10.5) * mm, "end": v(6.15, -16.84) * mm});
            skLineSegment(sketch, "E4.2.4.3", {"start": v(-4.85, -10.5) * mm, "end": v(2.49, -10.5) * mm});
            skLineSegment(sketch, "E4.2.4.4", {"start": v(-8.51, -16.84) * mm, "end": v(-4.85, -10.5) * mm});
            skLineSegment(sketch, "E4.2.4.5", {"start": v(-4.85, -23.2) * mm, "end": v(-8.51, -16.84) * mm});
            skLineSegment(sketch, "E4.2.4.6", {"start": v(2.49, -23.2) * mm, "end": v(-4.85, -23.2) * mm});
            skCircle(sketch, "E4.2.4.7", {"center": v(-1.18, -16.84) * mm, "radius": 6.35 * mm, "construction": true});
            skPoint(sketch, "E4.2.5.0", {"position": v(-1.18, -37.08) * mm});
            skLineSegment(sketch, "E4.2.5.1", {"start": v(6.15, -30.73) * mm, "end": v(2.49, -37.08) * mm});
            skLineSegment(sketch, "E4.2.5.2", {"start": v(2.49, -24.38) * mm, "end": v(6.15, -30.73) * mm});
            skLineSegment(sketch, "E4.2.5.3", {"start": v(-4.85, -24.38) * mm, "end": v(2.49, -24.38) * mm});
            skLineSegment(sketch, "E4.2.5.4", {"start": v(-8.51, -30.73) * mm, "end": v(-4.85, -24.38) * mm});
            skLineSegment(sketch, "E4.2.5.5", {"start": v(-4.85, -37.08) * mm, "end": v(-8.51, -30.73) * mm});
            skLineSegment(sketch, "E4.2.5.6", {"start": v(2.49, -37.08) * mm, "end": v(-4.85, -37.08) * mm});
            skCircle(sketch, "E4.2.5.7", {"center": v(-1.18, -30.73) * mm, "radius": 6.35 * mm, "construction": true});
            skPoint(sketch, "E4.3.0.0", {"position": v(22.85, 32.38) * mm});
            skLineSegment(sketch, "E4.3.0.1", {"start": v(30.18, 38.74) * mm, "end": v(26.51, 32.39) * mm});
            skLineSegment(sketch, "E4.3.0.2", {"start": v(26.51, 45.09) * mm, "end": v(30.18, 38.74) * mm});
            skLineSegment(sketch, "E4.3.0.3", {"start": v(19.18, 45.09) * mm, "end": v(26.51, 45.09) * mm});
            skLineSegment(sketch, "E4.3.0.4", {"start": v(15.52, 38.74) * mm, "end": v(19.18, 45.09) * mm});
            skLineSegment(sketch, "E4.3.0.5", {"start": v(19.18, 32.39) * mm, "end": v(15.52, 38.73) * mm});
            skLineSegment(sketch, "E4.3.0.6", {"start": v(26.51, 32.38) * mm, "end": v(19.18, 32.38) * mm});
            skCircle(sketch, "E4.3.0.7", {"center": v(22.85, 38.73) * mm, "radius": 6.35 * mm, "construction": true});
            skPoint(sketch, "E4.3.1.0", {"position": v(22.85, 18.5) * mm});
            skLineSegment(sketch, "E4.3.1.1", {"start": v(30.18, 24.84) * mm, "end": v(26.51, 18.5) * mm});
            skLineSegment(sketch, "E4.3.1.2", {"start": v(26.51, 31.2) * mm, "end": v(30.18, 24.84) * mm});
            skLineSegment(sketch, "E4.3.1.3", {"start": v(19.18, 31.2) * mm, "end": v(26.51, 31.2) * mm});
            skLineSegment(sketch, "E4.3.1.4", {"start": v(15.52, 24.84) * mm, "end": v(19.18, 31.2) * mm});
            skLineSegment(sketch, "E4.3.1.5", {"start": v(19.18, 18.5) * mm, "end": v(15.52, 24.84) * mm});
            skLineSegment(sketch, "E4.3.1.6", {"start": v(26.51, 18.5) * mm, "end": v(19.18, 18.5) * mm});
            skCircle(sketch, "E4.3.1.7", {"center": v(22.85, 24.84) * mm, "radius": 6.35 * mm, "construction": true});
            skPoint(sketch, "E4.3.2.0", {"position": v(22.85, 4.6) * mm});
            skLineSegment(sketch, "E4.3.2.1", {"start": v(30.18, 10.95) * mm, "end": v(26.51, 4.6) * mm});
            skLineSegment(sketch, "E4.3.2.2", {"start": v(26.51, 17.3) * mm, "end": v(30.18, 10.95) * mm});
            skLineSegment(sketch, "E4.3.2.3", {"start": v(19.18, 17.3) * mm, "end": v(26.51, 17.3) * mm});
            skLineSegment(sketch, "E4.3.2.4", {"start": v(15.52, 10.95) * mm, "end": v(19.18, 17.3) * mm});
            skLineSegment(sketch, "E4.3.2.5", {"start": v(19.18, 4.6) * mm, "end": v(15.52, 10.95) * mm});
            skLineSegment(sketch, "E4.3.2.6", {"start": v(26.51, 4.6) * mm, "end": v(19.18, 4.6) * mm});
            skCircle(sketch, "E4.3.2.7", {"center": v(22.85, 10.95) * mm, "radius": 6.35 * mm, "construction": true});
            skPoint(sketch, "E4.3.3.0", {"position": v(22.85, -9.3) * mm});
            skLineSegment(sketch, "E4.3.3.1", {"start": v(30.18, -2.95) * mm, "end": v(26.51, -9.3) * mm});
            skLineSegment(sketch, "E4.3.3.2", {"start": v(26.51, 3.4) * mm, "end": v(30.18, -2.95) * mm});
            skLineSegment(sketch, "E4.3.3.3", {"start": v(19.18, 3.4) * mm, "end": v(26.51, 3.4) * mm});
            skLineSegment(sketch, "E4.3.3.4", {"start": v(15.52, -2.95) * mm, "end": v(19.18, 3.4) * mm});
            skLineSegment(sketch, "E4.3.3.5", {"start": v(19.18, -9.3) * mm, "end": v(15.52, -2.95) * mm});
            skLineSegment(sketch, "E4.3.3.6", {"start": v(26.51, -9.3) * mm, "end": v(19.18, -9.3) * mm});
            skCircle(sketch, "E4.3.3.7", {"center": v(22.85, -2.95) * mm, "radius": 6.35 * mm, "construction": true});
            skPoint(sketch, "E4.3.4.0", {"position": v(22.85, -23.2) * mm});
            skLineSegment(sketch, "E4.3.4.1", {"start": v(30.18, -16.84) * mm, "end": v(26.51, -23.2) * mm});
            skLineSegment(sketch, "E4.3.4.2", {"start": v(26.51, -10.5) * mm, "end": v(30.18, -16.84) * mm});
            skLineSegment(sketch, "E4.3.4.3", {"start": v(19.18, -10.5) * mm, "end": v(26.51, -10.5) * mm});
            skLineSegment(sketch, "E4.3.4.4", {"start": v(15.52, -16.84) * mm, "end": v(19.18, -10.5) * mm});
            skLineSegment(sketch, "E4.3.4.5", {"start": v(19.18, -23.2) * mm, "end": v(15.52, -16.84) * mm});
            skLineSegment(sketch, "E4.3.4.6", {"start": v(26.51, -23.2) * mm, "end": v(19.18, -23.2) * mm});
            skCircle(sketch, "E4.3.4.7", {"center": v(22.85, -16.84) * mm, "radius": 6.35 * mm, "construction": true});
            skPoint(sketch, "E4.3.5.0", {"position": v(22.85, -37.08) * mm});
            skLineSegment(sketch, "E4.3.5.1", {"start": v(30.18, -30.73) * mm, "end": v(26.51, -37.08) * mm});
            skLineSegment(sketch, "E4.3.5.2", {"start": v(26.51, -24.38) * mm, "end": v(30.18, -30.73) * mm});
            skLineSegment(sketch, "E4.3.5.3", {"start": v(19.18, -24.38) * mm, "end": v(26.51, -24.38) * mm});
            skLineSegment(sketch, "E4.3.5.4", {"start": v(15.52, -30.73) * mm, "end": v(19.18, -24.38) * mm});
            skLineSegment(sketch, "E4.3.5.5", {"start": v(19.18, -37.08) * mm, "end": v(15.52, -30.73) * mm});
            skLineSegment(sketch, "E4.3.5.6", {"start": v(26.51, -37.08) * mm, "end": v(19.18, -37.08) * mm});
            skCircle(sketch, "E4.3.5.7", {"center": v(22.85, -30.73) * mm, "radius": 6.35 * mm, "construction": true});
            skPoint(sketch, "E4.4.0.0", {"position": v(46.88, 32.38) * mm});
            skLineSegment(sketch, "E4.4.0.1", {"start": v(54.2, 38.74) * mm, "end": v(50.54, 32.39) * mm});
            skLineSegment(sketch, "E4.4.0.2", {"start": v(50.54, 45.09) * mm, "end": v(54.2, 38.74) * mm});
            skLineSegment(sketch, "E4.4.0.3", {"start": v(43.21, 45.09) * mm, "end": v(50.54, 45.09) * mm});
            skLineSegment(sketch, "E4.4.0.4", {"start": v(39.54, 38.74) * mm, "end": v(43.21, 45.09) * mm});
            skLineSegment(sketch, "E4.4.0.5", {"start": v(43.21, 32.39) * mm, "end": v(39.54, 38.73) * mm});
            skLineSegment(sketch, "E4.4.0.6", {"start": v(50.54, 32.38) * mm, "end": v(43.21, 32.38) * mm});
            skCircle(sketch, "E4.4.0.7", {"center": v(46.88, 38.73) * mm, "radius": 6.35 * mm, "construction": true});
            skPoint(sketch, "E4.4.1.0", {"position": v(46.88, 18.5) * mm});
            skLineSegment(sketch, "E4.4.1.1", {"start": v(54.2, 24.84) * mm, "end": v(50.54, 18.5) * mm});
            skLineSegment(sketch, "E4.4.1.2", {"start": v(50.54, 31.2) * mm, "end": v(54.2, 24.84) * mm});
            skLineSegment(sketch, "E4.4.1.3", {"start": v(43.21, 31.2) * mm, "end": v(50.54, 31.2) * mm});
            skLineSegment(sketch, "E4.4.1.4", {"start": v(39.54, 24.84) * mm, "end": v(43.21, 31.2) * mm});
            skLineSegment(sketch, "E4.4.1.5", {"start": v(43.21, 18.5) * mm, "end": v(39.54, 24.84) * mm});
            skLineSegment(sketch, "E4.4.1.6", {"start": v(50.54, 18.5) * mm, "end": v(43.21, 18.5) * mm});
            skCircle(sketch, "E4.4.1.7", {"center": v(46.88, 24.84) * mm, "radius": 6.35 * mm, "construction": true});
            skPoint(sketch, "E4.4.2.0", {"position": v(46.88, 4.6) * mm});
            skLineSegment(sketch, "E4.4.2.1", {"start": v(54.2, 10.95) * mm, "end": v(50.54, 4.6) * mm});
            skLineSegment(sketch, "E4.4.2.2", {"start": v(50.54, 17.3) * mm, "end": v(54.2, 10.95) * mm});
            skLineSegment(sketch, "E4.4.2.3", {"start": v(43.21, 17.3) * mm, "end": v(50.54, 17.3) * mm});
            skLineSegment(sketch, "E4.4.2.4", {"start": v(39.54, 10.95) * mm, "end": v(43.21, 17.3) * mm});
            skLineSegment(sketch, "E4.4.2.5", {"start": v(43.21, 4.6) * mm, "end": v(39.54, 10.95) * mm});
            skLineSegment(sketch, "E4.4.2.6", {"start": v(50.54, 4.6) * mm, "end": v(43.21, 4.6) * mm});
            skCircle(sketch, "E4.4.2.7", {"center": v(46.88, 10.95) * mm, "radius": 6.35 * mm, "construction": true});
            skPoint(sketch, "E4.4.3.0", {"position": v(46.88, -9.3) * mm});
            skLineSegment(sketch, "E4.4.3.1", {"start": v(54.2, -2.95) * mm, "end": v(50.54, -9.3) * mm});
            skLineSegment(sketch, "E4.4.3.2", {"start": v(50.54, 3.4) * mm, "end": v(54.2, -2.95) * mm});
            skLineSegment(sketch, "E4.4.3.3", {"start": v(43.21, 3.4) * mm, "end": v(50.54, 3.4) * mm});
            skLineSegment(sketch, "E4.4.3.4", {"start": v(39.54, -2.95) * mm, "end": v(43.21, 3.4) * mm});
            skLineSegment(sketch, "E4.4.3.5", {"start": v(43.21, -9.3) * mm, "end": v(39.54, -2.95) * mm});
            skLineSegment(sketch, "E4.4.3.6", {"start": v(50.54, -9.3) * mm, "end": v(43.21, -9.3) * mm});
            skCircle(sketch, "E4.4.3.7", {"center": v(46.88, -2.95) * mm, "radius": 6.35 * mm, "construction": true});
            skPoint(sketch, "E4.4.4.0", {"position": v(46.88, -23.2) * mm});
            skLineSegment(sketch, "E4.4.4.1", {"start": v(54.2, -16.84) * mm, "end": v(50.54, -23.2) * mm});
            skLineSegment(sketch, "E4.4.4.2", {"start": v(50.54, -10.5) * mm, "end": v(54.2, -16.84) * mm});
            skLineSegment(sketch, "E4.4.4.3", {"start": v(43.21, -10.5) * mm, "end": v(50.54, -10.5) * mm});
            skLineSegment(sketch, "E4.4.4.4", {"start": v(39.54, -16.84) * mm, "end": v(43.21, -10.5) * mm});
            skLineSegment(sketch, "E4.4.4.5", {"start": v(43.21, -23.2) * mm, "end": v(39.54, -16.84) * mm});
            skLineSegment(sketch, "E4.4.4.6", {"start": v(50.54, -23.2) * mm, "end": v(43.21, -23.2) * mm});
            skCircle(sketch, "E4.4.4.7", {"center": v(46.88, -16.84) * mm, "radius": 6.35 * mm, "construction": true});
            skPoint(sketch, "E4.4.5.0", {"position": v(46.88, -37.08) * mm});
            skLineSegment(sketch, "E4.4.5.1", {"start": v(54.2, -30.73) * mm, "end": v(50.54, -37.08) * mm});
            skLineSegment(sketch, "E4.4.5.2", {"start": v(50.54, -24.38) * mm, "end": v(54.2, -30.73) * mm});
            skLineSegment(sketch, "E4.4.5.3", {"start": v(43.21, -24.38) * mm, "end": v(50.54, -24.38) * mm});
            skLineSegment(sketch, "E4.4.5.4", {"start": v(39.54, -30.73) * mm, "end": v(43.21, -24.38) * mm});
            skLineSegment(sketch, "E4.4.5.5", {"start": v(43.21, -37.08) * mm, "end": v(39.54, -30.73) * mm});
            skLineSegment(sketch, "E4.4.5.6", {"start": v(50.54, -37.08) * mm, "end": v(43.21, -37.08) * mm});
            skCircle(sketch, "E4.4.5.7", {"center": v(46.88, -30.73) * mm, "radius": 6.35 * mm, "construction": true});
            skLineSegment(sketch, "E4.direction1", {"start": v(-52.9, 32.38) * mm, "end": v(-28.88, 32.38) * mm, "construction": true});
            skLineSegment(sketch, "E4.direction2", {"start": v(-52.9, 32.38) * mm, "end": v(-52.9, 18.5) * mm, "construction": true});
            skSolve(sketch);
        }
        {
            var Q0;
            Q0 = qSketchRegion(id + "F2", true);
            extrude(context, id + "F3", {"entities" : qUnion([Q0]), "operationType" : NewBodyOperationType.REMOVE, "endBound" : BoundingType.THROUGH_ALL, "depth" : 25.4 * mm, "offsetDistance" : 25.4 * mm});
        }
        {
            var Q0;
            Q0=makeQuery(id+"F1.opExtrude","SWEPT_FACE",FACE,{"disambiguationData":[OSD([sQuery(id+"F0.wireOp",EDGE,"E0.left")])]});
            var sketch = newSketch(context, id + "F4", { "sketchPlane" : qUnion([Q0])});
            skLineSegment(sketch, "E5", {"start": v(-24.77, 31.75) * mm, "end": v(-12.45, 31.75) * mm});
            skLineSegment(sketch, "E6", {"start": v(-2.25, 22.63) * mm, "end": v(12.63, 63.5) * mm});
            skLineSegment(sketch, "E7", {"start": v(12.63, 63.5) * mm, "end": v(12.63, 67.53) * mm});
            skLineSegment(sketch, "E8", {"start": v(12.63, 67.53) * mm, "end": v(-63.5, 67.53) * mm});
            skLineSegment(sketch, "E9", {"start": v(-63.5, 67.53) * mm, "end": v(-63.5, -7.57) * mm});
            skLineSegment(sketch, "E10", {"start": v(-63.5, -7.57) * mm, "end": v(-39.08, -7.57) * mm});
            skLineSegment(sketch, "E11", {"start": v(-14.18, 26.98) * mm, "end": v(-2.25, 22.63) * mm});
            skLineSegment(sketch, "E12", {"start": v(-14.18, 26.98) * mm, "end": v(-12.45, 31.75) * mm});
            skLineSegment(sketch, "E13", {"start": v(-24.77, 31.75) * mm, "end": v(-39.08, -7.57) * mm});
            skSolve(sketch);
        }
        {
            var Q0;
            Q0 = qSketchRegion(id + "F4", true);
            extrude(context, id + "F5", {"entities" : qUnion([Q0]), "operationType" : NewBodyOperationType.REMOVE, "endBound" : BoundingType.THROUGH_ALL, "oppositeDirection" : true, "depth" : 25.4 * mm, "offsetDistance" : 25.4 * mm});
        }
        {
            var Q0;
            Q0=makeQuery(id+"F1.opExtrude","SWEPT_FACE",FACE,{"disambiguationData":[OSD([sQuery(id+"F0.wireOp",EDGE,"E0.left")])]});
            var sketch = newSketch(context, id + "F6", { "sketchPlane" : qUnion([Q0])});
            skLineSegment(sketch, "E14.0", {"start": v(-24.77, 31.75) * mm, "end": v(-36.32, 0) * mm});
            skLineSegment(sketch, "E15", {"start": v(-24.77, 31.75) * mm, "end": v(-26.12, 31.75) * mm});
            skLineSegment(sketch, "E16", {"start": v(-26.12, 31.75) * mm, "end": v(-37.67, 0) * mm});
            skLineSegment(sketch, "E17", {"start": v(-37.67, 0) * mm, "end": v(-36.32, 0) * mm});
            skSolve(sketch);
        }
        {
            var Q0;
            Q0 = qSketchRegion(id + "F6", true);
            var Q1;
            Q1=makeQuery(id+"F1.opExtrude","SWEPT_FACE",FACE,{"disambiguationData":[OSD([sQuery(id+"F0.wireOp",EDGE,"E0.right")])]});
            extrude(context, id + "F7", {"entities" : qUnion([Q0]), "operationType" : NewBodyOperationType.ADD, "endBound" : BoundingType.UP_TO_SURFACE, "oppositeDirection" : true, "depth" : 25.4 * mm, "endBoundEntityFace" : qUnion([Q1]), "offsetDistance" : 25.4 * mm});
        }
        {
            var Q0;
            Q0=makeQuery(id+"F1.opExtrude","CAP_FACE",FACE,{"disambiguationData":[OSD([sQuery(id+"F0.wireOp",EDGE,"E0.bottom"),sQuery(id+"F0.wireOp",EDGE,"E0.top"),sQuery(id+"F0.wireOp",EDGE,"E0.left"),sQuery(id+"F0.wireOp",EDGE,"E0.right")])],"isStart":false});
            var sketch = newSketch(context, id + "F8", { "sketchPlane" : qUnion([Q0])});
            skLineSegment(sketch, "E18", {"start": v(-78.08, -37.72) * mm, "end": v(79.49, -37.72) * mm});
            skLineSegment(sketch, "E19", {"start": v(79.49, -37.72) * mm, "end": v(79.49, -52.4) * mm});
            skLineSegment(sketch, "E20", {"start": v(79.49, -52.4) * mm, "end": v(-78.08, -52.4) * mm});
            skLineSegment(sketch, "E21", {"start": v(-78.08, -52.4) * mm, "end": v(-78.08, -37.72) * mm});
            skPoint(sketch, "E22.orphan", {"position": v(-68.58, -37.72) * mm});
            skSolve(sketch);
        }
        {
            var Q0;
            Q0 = qSketchRegion(id + "F8", true);
            extrude(context, id + "F9", {"entities" : qUnion([Q0]), "operationType" : NewBodyOperationType.REMOVE, "endBound" : BoundingType.THROUGH_ALL, "oppositeDirection" : true, "depth" : 25.4 * mm, "offsetDistance" : 25.4 * mm});
        }
        {
            var Q0;
            Q0=makeQuery(id+"F7.boolean.opBoolean","MERGE",FACE,{"derivedFrom":[makeQuery(id+"F1.opExtrude","SWEPT_FACE",FACE,{"disambiguationData":[OSD([sQuery(id+"F0.wireOp",EDGE,"E0.left")])]}),makeQuery(id+"F7.opExtrude","CAP_FACE",FACE,{"disambiguationData":[OSD([sQuery(id+"F6.wireOp",EDGE,"E14.0"),sQuery(id+"F6.wireOp",EDGE,"E15"),sQuery(id+"F6.wireOp",EDGE,"E16"),sQuery(id+"F6.wireOp",EDGE,"E17")])],"isStart":true})]});
            var sketch = newSketch(context, id + "F10", { "sketchPlane" : qUnion([Q0])});
            skLineSegment(sketch, "E23.0", {"start": v(37.72, 63.5) * mm, "end": v(37.72, 0) * mm});
            skLineSegment(sketch, "E24", {"start": v(37.72, 63.5) * mm, "end": v(38.99, 63.5) * mm});
            skLineSegment(sketch, "E25", {"start": v(38.99, 63.5) * mm, "end": v(38.99, 0) * mm});
            skLineSegment(sketch, "E26", {"start": v(38.99, 0) * mm, "end": v(37.72, 0) * mm});
            skSolve(sketch);
        }
        {
            var Q0;
            Q0 = qSketchRegion(id + "F10", true);
            var Q1;
            {var subQ0=sQuery(id+"F0.wireOp",EDGE,"E0.right");Q1=makeQuery(id+"F7.boolean.opBoolean","MERGE",FACE,{"derivedFrom":[makeQuery(id+"F1.opExtrude","SWEPT_FACE",FACE,{"disambiguationData":[OSD([subQ0])]}),makeQuery(id+"F7.opExtrude","CAP_FACE",FACE,{"disambiguationData":[OSD([subQ0])],"isStart":false})]});}
            extrude(context, id + "F11", {"entities" : qUnion([Q0]), "operationType" : NewBodyOperationType.ADD, "endBound" : BoundingType.UP_TO_SURFACE, "oppositeDirection" : true, "depth" : 25.4 * mm, "endBoundEntityFace" : qUnion([Q1]), "offsetDistance" : 25.4 * mm});
        }
        {
            var Q0;
            Q0=qCreatedBy(makeId("Top.planeOp"),FACE);
            var sketch = newSketch(context, id + "F12", { "sketchPlane" : qUnion([Q0])});
            skLineSegment(sketch, "E27", {"start": v(-51.98, -44.02) * mm, "end": v(-51.98, 44.88) * mm});
            skLineSegment(sketch, "E28", {"start": v(-51.98, 44.88) * mm, "end": v(-76.92, 44.88) * mm});
            skLineSegment(sketch, "E29", {"start": v(-76.92, 44.88) * mm, "end": v(-76.92, -44.02) * mm});
            skLineSegment(sketch, "E30", {"start": v(-76.92, -44.02) * mm, "end": v(-51.98, -44.02) * mm});
            skLineSegment(sketch, "E31", {"start": v(49.62, -44.02) * mm, "end": v(49.62, 44.88) * mm});
            skLineSegment(sketch, "E32", {"start": v(81.66, 44.88) * mm, "end": v(81.66, -44.02) * mm});
            skLineSegment(sketch, "E33", {"start": v(81.66, -44.02) * mm, "end": v(49.62, -44.02) * mm});
            skLineSegment(sketch, "E34", {"start": v(49.62, 44.88) * mm, "end": v(81.66, 44.88) * mm});
            skPoint(sketch, "E35.end.orphan", {"position": v(81.66, 35.29) * mm});
            skSolve(sketch);
        }
        {
            var Q0;
            Q0 = qSketchRegion(id + "F12", true);
            extrude(context, id + "F13", {"entities" : qUnion([Q0]), "operationType" : NewBodyOperationType.REMOVE, "endBound" : BoundingType.THROUGH_ALL, "depth" : 25.4 * mm, "offsetDistance" : 25.4 * mm});
        }
        {
            var Q0;
            Q0=makeQuery(id+"F13.boolean.opBoolean","COPY",FACE,{"disambiguationData":[TD([makeQuery(id+"F3.boolean.opBoolean","COPY",FACE,{"derivedFrom":makeQuery(id+"F3.opExtrude","SWEPT_FACE",FACE,{"disambiguationData":[OSD([sQuery(id+"F2.wireOp",EDGE,"E4.0.5.6")])]})})])],"derivedFrom":makeQuery(id+"F13.opExtrude","SWEPT_FACE",FACE,{"disambiguationData":[OSD([sQuery(id+"F12.wireOp",EDGE,"E27")])]})});
            var sketch = newSketch(context, id + "F14", { "sketchPlane" : qUnion([Q0])});
            skLineSegment(sketch, "E36", {"start": v(38.99, 0) * mm, "end": v(-37.67, 0) * mm});
            skLineSegment(sketch, "E37", {"start": v(-37.67, 0) * mm, "end": v(-26.12, 31.75) * mm});
            skLineSegment(sketch, "E38", {"start": v(-26.12, 31.75) * mm, "end": v(-12.45, 31.75) * mm});
            skLineSegment(sketch, "E39", {"start": v(12.63, 63.5) * mm, "end": v(38.99, 63.5) * mm});
            skLineSegment(sketch, "E40", {"start": v(38.99, 63.5) * mm, "end": v(38.99, 0) * mm});
            skLineSegment(sketch, "E41", {"start": v(12.63, 63.5) * mm, "end": v(-12.45, 31.75) * mm});
            skSolve(sketch);
        }
        {
            var Q0;
            Q0 = qSketchRegion(id + "F14", true);
            extrude(context, id + "F15", {"entities" : qUnion([Q0]), "operationType" : NewBodyOperationType.ADD, "oppositeDirection" : true, "depth" : 1.27 * mm, "offsetDistance" : 25.4 * mm});
        }
        {
            var Q0;
            Q0=makeQuery(id+"F13.boolean.opBoolean","COPY",FACE,{"disambiguationData":[TD([makeQuery(id+"F3.boolean.opBoolean","COPY",FACE,{"derivedFrom":makeQuery(id+"F3.opExtrude","SWEPT_FACE",FACE,{"disambiguationData":[OSD([sQuery(id+"F2.wireOp",EDGE,"E4.4.0.6")])]})})])],"derivedFrom":makeQuery(id+"F13.opExtrude","SWEPT_FACE",FACE,{"disambiguationData":[OSD([sQuery(id+"F12.wireOp",EDGE,"E31")])]})});
            var sketch = newSketch(context, id + "F16", { "sketchPlane" : qUnion([Q0])});
            skLineSegment(sketch, "E42.0.0", {"start": v(26.12, 31.75) * mm, "end": v(37.67, 0) * mm});
            skLineSegment(sketch, "E42.0.1", {"start": v(37.67, 0) * mm, "end": v(-38.99, 0) * mm});
            skLineSegment(sketch, "E42.0.2", {"start": v(-38.99, 0) * mm, "end": v(-38.99, 63.5) * mm});
            skLineSegment(sketch, "E42.0.3", {"start": v(-38.99, 63.5) * mm, "end": v(-12.63, 63.5) * mm});
            skLineSegment(sketch, "E42.0.4", {"start": v(-12.63, 63.5) * mm, "end": v(12.45, 31.75) * mm});
            skLineSegment(sketch, "E42.0.5", {"start": v(12.45, 31.75) * mm, "end": v(26.12, 31.75) * mm});
            skSolve(sketch);
        }
        {
            var Q0;
            Q0 = qSketchRegion(id + "F16", true);
            extrude(context, id + "F17", {"entities" : qUnion([Q0]), "operationType" : NewBodyOperationType.ADD, "oppositeDirection" : true, "depth" : 1.27 * mm, "offsetDistance" : 25.4 * mm});
        }
        {
            var Q0;
            Q0=qCreatedBy(makeId("Top.planeOp"),FACE);
            var sketch = newSketch(context, id + "F18", { "sketchPlane" : qUnion([Q0])});
            skLineSegment(sketch, "E43", {"start": v(-57.7, -42.56) * mm, "end": v(-57.7, 45.12) * mm});
            skLineSegment(sketch, "E44", {"start": v(-57.7, 45.12) * mm, "end": v(60.45, 45.12) * mm});
            skLineSegment(sketch, "E45", {"start": v(60.45, 45.12) * mm, "end": v(60.45, -42.56) * mm});
            skLineSegment(sketch, "E46", {"start": v(60.45, -42.56) * mm, "end": v(-57.7, -42.56) * mm});
            skSolve(sketch);
        }
        {
            var Q0;
            Q0 = qSketchRegion(id + "F18", true);
            extrude(context, id + "F19", {"entities" : qUnion([Q0]), "operationType" : NewBodyOperationType.REMOVE, "depth" : 15.88 * mm, "offsetDistance" : 25.4 * mm});
        }
        {
            var Q0;
            Q0=makeQuery(id+"F7.opExtrude","SWEPT_FACE",FACE,{"disambiguationData":[OSD([sQuery(id+"F6.wireOp",EDGE,"E16")])]});
            var sketch = newSketch(context, id + "F20", { "sketchPlane" : qUnion([Q0])});
            skLineSegment(sketch, "E47", {"start": v(-10.83, 15.97) * mm, "end": v(-12.79, 10.43) * mm});
            skLineSegment(sketch, "E48", {"start": v(-12.79, 10.43) * mm, "end": v(-11.39, 10.43) * mm});
            skLineSegment(sketch, "E49", {"start": v(-11.39, 10.43) * mm, "end": v(-9.43, 15.97) * mm});
            skLineSegment(sketch, "E50", {"start": v(-9.43, 15.97) * mm, "end": v(-10.83, 15.97) * mm});
            skLineSegment(sketch, "E51", {"start": v(-9.17, 14.95) * mm, "end": v(-10.77, 10.43) * mm});
            skLineSegment(sketch, "E52", {"start": v(-10.77, 10.43) * mm, "end": v(-9.42, 10.43) * mm});
            skLineSegment(sketch, "E53", {"start": v(-9.42, 10.43) * mm, "end": v(-8.17, 13.96) * mm});
            skLineSegment(sketch, "E54", {"start": v(-9.17, 14.95) * mm, "end": v(-7.75, 14.95) * mm});
            skLineSegment(sketch, "E55", {"start": v(-7.75, 14.95) * mm, "end": v(-7.88, 14.58) * mm});
            skLineSegment(sketch, "E56", {"start": v(-7.72, 13.93) * mm, "end": v(-8.96, 10.43) * mm});
            skLineSegment(sketch, "E57", {"start": v(-8.96, 10.43) * mm, "end": v(-7.6, 10.43) * mm});
            skFitSpline(sketch, "E58", {"points": [v(-7.6, 10.43) * mm, v(-7.13, 11.7) * mm, v(-6.58, 13.3) * mm, v(-6.34, 14.04) * mm, v(-6.27, 14.43) * mm, v(-6.36, 14.73) * mm, v(-6.6, 14.93) * mm, v(-6.77, 14.99) * mm, v(-7.17, 14.95) * mm, v(-7.57, 14.78) * mm, v(-7.76, 14.66) * mm, v(-7.88, 14.58) * mm], "startDerivative": vector(3.12, 8.55) * mm, "endDerivative": vector(-2.77, -1.14) * mm});
            skFitSpline(sketch, "E59", {"points": [v(-8.17, 13.96) * mm, v(-8.08, 14.09) * mm, v(-7.88, 14.17) * mm, v(-7.71, 14.09) * mm, v(-7.72, 13.93) * mm], "startDerivative": vector(0.29, 0.48) * mm, "endDerivative": vector(-0.04, -0.6) * mm});
            skPoint(sketch, "E60.orphan", {"position": v(-7.61, 10.43) * mm});
            skCircle(sketch, "E61", {"center": v(-9.87, 17.13) * mm, "radius": 0.73 * mm});
            skPoint(sketch, "E61.first.point", {"position": v(-10.49, 17.52) * mm});
            skPoint(sketch, "E61.second.point", {"position": v(-9.21, 17.44) * mm});
            skPoint(sketch, "E61.third.point", {"position": v(-9.82, 16.4) * mm});
            skLineSegment(sketch, "E62", {"start": v(-5.52, 14.95) * mm, "end": v(-7.1, 10.43) * mm});
            skLineSegment(sketch, "E63", {"start": v(-7.1, 10.43) * mm, "end": v(-5.76, 10.43) * mm});
            skLineSegment(sketch, "E64", {"start": v(-5.76, 10.43) * mm, "end": v(-4.5, 14.02) * mm});
            skLineSegment(sketch, "E65", {"start": v(-5.52, 14.95) * mm, "end": v(-4.1, 14.95) * mm});
            skLineSegment(sketch, "E66", {"start": v(-4.1, 14.95) * mm, "end": v(-4.23, 14.59) * mm});
            skLineSegment(sketch, "E67", {"start": v(-4.05, 14) * mm, "end": v(-5.3, 10.43) * mm});
            skLineSegment(sketch, "E68", {"start": v(-5.3, 10.43) * mm, "end": v(-3.93, 10.43) * mm});
            skFitSpline(sketch, "E69", {"points": [v(-3.93, 10.43) * mm, v(-3.47, 11.7) * mm, v(-2.9, 13.3) * mm, v(-2.65, 14.04) * mm, v(-2.59, 14.43) * mm, v(-2.67, 14.73) * mm, v(-2.9, 14.93) * mm, v(-3.08, 14.99) * mm, v(-3.48, 14.95) * mm, v(-3.89, 14.78) * mm, v(-4.07, 14.68) * mm, v(-4.23, 14.59) * mm], "startDerivative": vector(3.12, 8.55) * mm, "endDerivative": vector(-2.77, -1.13) * mm});
            skFitSpline(sketch, "E70", {"points": [v(-4.5, 14.02) * mm, v(-4.41, 14.14) * mm, v(-4.24, 14.2) * mm, v(-4.08, 14.14) * mm, v(-4.05, 14) * mm], "startDerivative": vector(0.29, 0.48) * mm, "endDerivative": vector(-0.04, -0.6) * mm});
            skLineSegment(sketch, "E71", {"start": v(8.39, 14.95) * mm, "end": v(6.79, 10.43) * mm});
            skLineSegment(sketch, "E72", {"start": v(6.79, 10.43) * mm, "end": v(8.13, 10.43) * mm});
            skLineSegment(sketch, "E73", {"start": v(8.13, 10.43) * mm, "end": v(9.35, 13.87) * mm});
            skLineSegment(sketch, "E74", {"start": v(8.39, 14.95) * mm, "end": v(9.8, 14.95) * mm});
            skLineSegment(sketch, "E75", {"start": v(9.8, 14.95) * mm, "end": v(9.64, 14.48) * mm});
            skLineSegment(sketch, "E76", {"start": v(9.8, 13.84) * mm, "end": v(8.6, 10.43) * mm});
            skLineSegment(sketch, "E77", {"start": v(8.6, 10.43) * mm, "end": v(9.97, 10.43) * mm});
            skFitSpline(sketch, "E78", {"points": [v(9.93, 10.33) * mm, v(10.38, 11.61) * mm, v(10.95, 13.2) * mm, v(11.2, 13.95) * mm, v(11.26, 14.33) * mm, v(11.18, 14.64) * mm, v(10.94, 14.83) * mm, v(10.76, 14.9) * mm, v(10.37, 14.85) * mm, v(9.96, 14.68) * mm, v(9.77, 14.56) * mm, v(9.64, 14.48) * mm], "startDerivative": vector(3.12, 8.55) * mm, "endDerivative": vector(-2.77, -1.14) * mm});
            skFitSpline(sketch, "E79", {"points": [v(9.35, 13.87) * mm, v(9.45, 14.02) * mm, v(9.6, 14.1) * mm, v(9.77, 14.05) * mm, v(9.8, 13.84) * mm], "startDerivative": vector(0.29, 0.48) * mm, "endDerivative": vector(-0.04, -0.6) * mm});
            skLineSegment(sketch, "E80", {"start": v(-12.79, 10.43) * mm, "end": v(4.97, 10.43) * mm, "construction": true});
            skFitSpline(sketch, "E81", {"points": [v(-2.4, 13.43) * mm, v(-2.1, 14.03) * mm, v(-1.9, 14.32) * mm, v(-1.69, 14.5) * mm, v(-1.44, 14.66) * mm, v(-1.2, 14.78) * mm, v(-0.87, 14.88) * mm, v(-0.55, 14.92) * mm, v(-0.1, 14.92) * mm, v(0.38, 14.8) * mm, v(0.73, 14.54) * mm, v(0.88, 14.2) * mm, v(0.9, 13.97) * mm, v(0.76, 13.4) * mm, v(0.45, 12.41) * mm, v(0.17, 11.7) * mm, v(0, 11.24) * mm, v(-0.21, 10.95) * mm, v(-0.5, 10.7) * mm, v(-0.85, 10.5) * mm, v(-1.16, 10.37) * mm, v(-1.54, 10.27) * mm, v(-2, 10.23) * mm, v(-2.45, 10.27) * mm, v(-2.77, 10.38) * mm, v(-3.01, 10.6) * mm, v(-3.07, 10.72) * mm, v(-3.12, 10.92) * mm, v(-3.1, 11.26) * mm, v(-3, 11.65) * mm, v(-2.77, 12.5) * mm, v(-2.4, 13.43) * mm]});
            skFitSpline(sketch, "E82", {"points": [v(-1.18, 12.94) * mm, v(-1.5, 12.12) * mm, v(-1.71, 11.49) * mm, v(-1.79, 11.29) * mm, v(-1.8, 11.17) * mm, v(-1.8, 11.1) * mm, v(-1.74, 11.06) * mm, v(-1.67, 11.03) * mm, v(-1.6, 11.03) * mm, v(-1.53, 11.06) * mm, v(-1.44, 11.15) * mm, v(-1.38, 11.24) * mm, v(-1.28, 11.5) * mm, v(-0.9, 12.61) * mm, v(-0.63, 13.36) * mm, v(-0.48, 13.8) * mm, v(-0.45, 13.92) * mm, v(-0.46, 14.04) * mm, v(-0.5, 14.1) * mm, v(-0.57, 14.12) * mm, v(-0.63, 14.11) * mm, v(-0.7, 14.08) * mm, v(-0.75, 14.04) * mm, v(-0.79, 14) * mm, v(-0.83, 13.91) * mm, v(-1, 13.46) * mm, v(-1.18, 12.94) * mm]});
            skLineSegment(sketch, "E83", {"start": v(1.4, 14.95) * mm, "end": v(2.65, 14.95) * mm});
            skLineSegment(sketch, "E84", {"start": v(2.65, 14.95) * mm, "end": v(1.92, 11.76) * mm});
            skLineSegment(sketch, "E85", {"start": v(1.92, 11.76) * mm, "end": v(3.3, 14.95) * mm});
            skLineSegment(sketch, "E86", {"start": v(3.3, 14.95) * mm, "end": v(4.55, 14.95) * mm});
            skLineSegment(sketch, "E87", {"start": v(4.55, 14.95) * mm, "end": v(2.3, 10.43) * mm});
            skLineSegment(sketch, "E88", {"start": v(2.3, 10.43) * mm, "end": v(0.53, 10.43) * mm});
            skLineSegment(sketch, "E89", {"start": v(0.53, 10.43) * mm, "end": v(1.4, 14.95) * mm});
            skFitSpline(sketch, "E90", {"points": [v(4.24, 13.41) * mm, v(4.52, 14.02) * mm, v(4.74, 14.31) * mm, v(4.94, 14.49) * mm, v(5.2, 14.65) * mm, v(5.44, 14.77) * mm, v(5.77, 14.87) * mm, v(6.09, 14.9) * mm, v(6.52, 14.91) * mm, v(7.01, 14.8) * mm, v(7.36, 14.53) * mm, v(7.51, 14.19) * mm, v(7.52, 13.96) * mm, v(7.4, 13.4) * mm, v(6.8, 11.68) * mm, v(6.62, 11.23) * mm, v(6.42, 10.94) * mm, v(6.13, 10.7) * mm, v(5.78, 10.48) * mm, v(5.47, 10.35) * mm, v(5.1, 10.26) * mm, v(4.63, 10.22) * mm, v(4.18, 10.26) * mm, v(3.86, 10.37) * mm, v(3.62, 10.6) * mm, v(3.57, 10.7) * mm, v(3.52, 10.9) * mm, v(3.54, 11.24) * mm, v(3.63, 11.64) * mm, v(3.86, 12.48) * mm, v(4.24, 13.41) * mm]});
            skFitSpline(sketch, "E91", {"points": [v(5.11, 12.06) * mm, v(4.88, 11.43) * mm, v(4.8, 11.23) * mm, v(4.78, 11.11) * mm, v(4.8, 11.04) * mm, v(4.85, 11) * mm, v(4.92, 10.97) * mm, v(4.98, 10.97) * mm, v(5.06, 11) * mm, v(5.14, 11.04) * mm, v(5.23, 11.17) * mm, v(5.36, 11.42) * mm, v(6.16, 13.7) * mm, v(6.17, 13.83) * mm, v(6.2, 13.93) * mm, v(6.16, 14) * mm, v(6.1, 14.05) * mm, v(6.03, 14.05) * mm, v(5.94, 14) * mm, v(5.9, 13.96) * mm, v(5.86, 13.91) * mm, v(5.78, 13.75) * mm, v(5.63, 13.4) * mm, v(5.11, 12.06) * mm]});
            skLineSegment(sketch, "E92", {"start": v(6.97, 12.14) * mm, "end": v(5.64, 12.14) * mm});
            skLineSegment(sketch, "E93", {"start": v(7.07, 12.44) * mm, "end": v(5.26, 12.44) * mm});
            skLineSegment(sketch, "E94", {"start": v(5.55, 13.2) * mm, "end": v(6, 13.2) * mm});
            skPoint(sketch, "E95.orphan", {"position": v(5.94, 13.2) * mm});
            skLineSegment(sketch, "E96", {"start": v(11.92, 13.86) * mm, "end": v(11.46, 13.86) * mm});
            skLineSegment(sketch, "E97", {"start": v(11.46, 13.86) * mm, "end": v(11.73, 14.6) * mm});
            skLineSegment(sketch, "E98", {"start": v(11.73, 14.6) * mm, "end": v(12.05, 14.6) * mm});
            skLineSegment(sketch, "E99", {"start": v(12.05, 14.6) * mm, "end": v(12.3, 15.29) * mm});
            skLineSegment(sketch, "E100", {"start": v(12.3, 15.29) * mm, "end": v(13.54, 15.29) * mm});
            skLineSegment(sketch, "E101", {"start": v(13.54, 15.29) * mm, "end": v(13.3, 14.6) * mm});
            skLineSegment(sketch, "E102", {"start": v(13.3, 14.6) * mm, "end": v(13.8, 14.6) * mm});
            skLineSegment(sketch, "E103", {"start": v(13.8, 14.6) * mm, "end": v(13.53, 13.86) * mm});
            skLineSegment(sketch, "E104", {"start": v(13.53, 13.86) * mm, "end": v(13.03, 13.86) * mm});
            skLineSegment(sketch, "E105", {"start": v(13.03, 13.86) * mm, "end": v(12.07, 11.16) * mm});
            skLineSegment(sketch, "E106", {"start": v(12.07, 11.16) * mm, "end": v(12.53, 11.16) * mm});
            skLineSegment(sketch, "E107", {"start": v(12.53, 11.16) * mm, "end": v(12.23, 10.43) * mm});
            skFitSpline(sketch, "E108", {"points": [v(11.92, 13.85) * mm, v(11.47, 12.69) * mm, v(11.17, 11.85) * mm, v(10.93, 11.15) * mm, v(10.87, 10.97) * mm, v(10.82, 10.82) * mm, v(10.8, 10.66) * mm, v(10.84, 10.57) * mm, v(10.87, 10.52) * mm, v(11, 10.46) * mm, v(11.18, 10.44) * mm, v(11.42, 10.42) * mm], "startDerivative": vector(-2.36, -6.2) * mm, "endDerivative": vector(4.33, 0.18) * mm});
            skLineSegment(sketch, "E109", {"start": v(-9.4, 9.83) * mm, "end": v(-12.7, 9.83) * mm});
            skFitSpline(sketch, "E110", {"points": [v(-12.7, 9.83) * mm, v(-12.53, 9.43) * mm, v(-12.2, 8.85) * mm, v(-11.77, 8.2) * mm, v(-10.98, 7.35) * mm, v(-10.05, 6.6) * mm, v(-8.85, 5.94) * mm, v(-7.63, 5.48) * mm, v(-6.16, 5.2) * mm, v(-5.36, 5.13) * mm, v(-4.13, 5.15) * mm, v(-2.42, 5.4) * mm, v(-1.14, 5.78) * mm, v(0.15, 6.3) * mm, v(0.93, 6.68) * mm, v(2.15, 7.46) * mm, v(2.81, 7.96) * mm, v(3.33, 8.4) * mm, v(4.03, 9.04) * mm, v(4.84, 9.95) * mm], "startDerivative": vector(4.48, -11.52) * mm, "endDerivative": vector(14.45, 16.85) * mm});
            skFitSpline(sketch, "E111", {"points": [v(4.84, 9.95) * mm, v(4.39, 9.65) * mm, v(3.75, 9.22) * mm, v(3.36, 8.98) * mm, v(2.38, 8.4) * mm, v(1.17, 7.8) * mm, v(-0.1, 7.32) * mm, v(-1.06, 7.04) * mm, v(-2.43, 6.81) * mm, v(-3.23, 6.79) * mm, v(-4.18, 6.86) * mm, v(-5.32, 7.07) * mm, v(-6.33, 7.42) * mm, v(-7.2, 7.85) * mm, v(-7.73, 8.18) * mm, v(-8.45, 8.73) * mm, v(-8.91, 9.17) * mm, v(-9.2, 9.53) * mm, v(-9.31, 9.68) * mm, v(-9.4, 9.83) * mm], "startDerivative": vector(-9.63, -6.37) * mm, "endDerivative": vector(-3.18, 6.42) * mm});
            skFitSpline(sketch, "E112", {"points": [v(10.53, 15.12) * mm, v(10.87, 15.49) * mm, v(11.41, 16.01) * mm, v(12.15, 16.74) * mm, v(13.25, 17.77) * mm, v(14.02, 18.43) * mm, v(14.87, 19.11) * mm, v(15.8, 19.77) * mm, v(16.36, 20.02) * mm, v(16.66, 20.04) * mm, v(16.93, 19.97) * mm, v(17.07, 19.82) * mm, v(17.17, 19.57) * mm, v(17.2, 19.4) * mm, v(17.2, 18.85) * mm, v(17.1, 18.5) * mm], "startDerivative": vector(5.25, 5.78) * mm, "endDerivative": vector(-2.32, -5.9) * mm});
            skLineSegment(sketch, "E113", {"start": v(17.1, 18.5) * mm, "end": v(15.52, 16.66) * mm});
            skFitSpline(sketch, "E114", {"points": [v(15.52, 16.66) * mm, v(15.63, 16.91) * mm, v(15.65, 17.33) * mm, v(15.61, 17.58) * mm, v(15.45, 17.8) * mm, v(15.33, 17.9) * mm, v(15.21, 17.98) * mm, v(14.95, 18.02) * mm, v(14.64, 17.95) * mm, v(14.25, 17.8) * mm, v(13.67, 17.47) * mm, v(12.74, 16.87) * mm, v(11.92, 16.26) * mm, v(10.53, 15.12) * mm], "startDerivative": vector(2.03, 3.92) * mm, "endDerivative": vector(-9.95, -8.23) * mm});
            skLineSegment(sketch, "E115", {"start": v(12.23, 10.43) * mm, "end": v(11.42, 10.42) * mm});
            skLineSegment(sketch, "E116", {"start": v(11.77, 13.47) * mm, "end": v(11.92, 13.86) * mm});
            skSolve(sketch);
        }
        {
            var Q0;
            Q0 = qSketchRegion(id + "F20", true);
            extrude(context, id + "F21", {"entities" : qUnion([Q0]), "operationType" : NewBodyOperationType.REMOVE, "oppositeDirection" : true, "depth" : 0.5 * mm, "offsetDistance" : 25.4 * mm});
        }
    });
